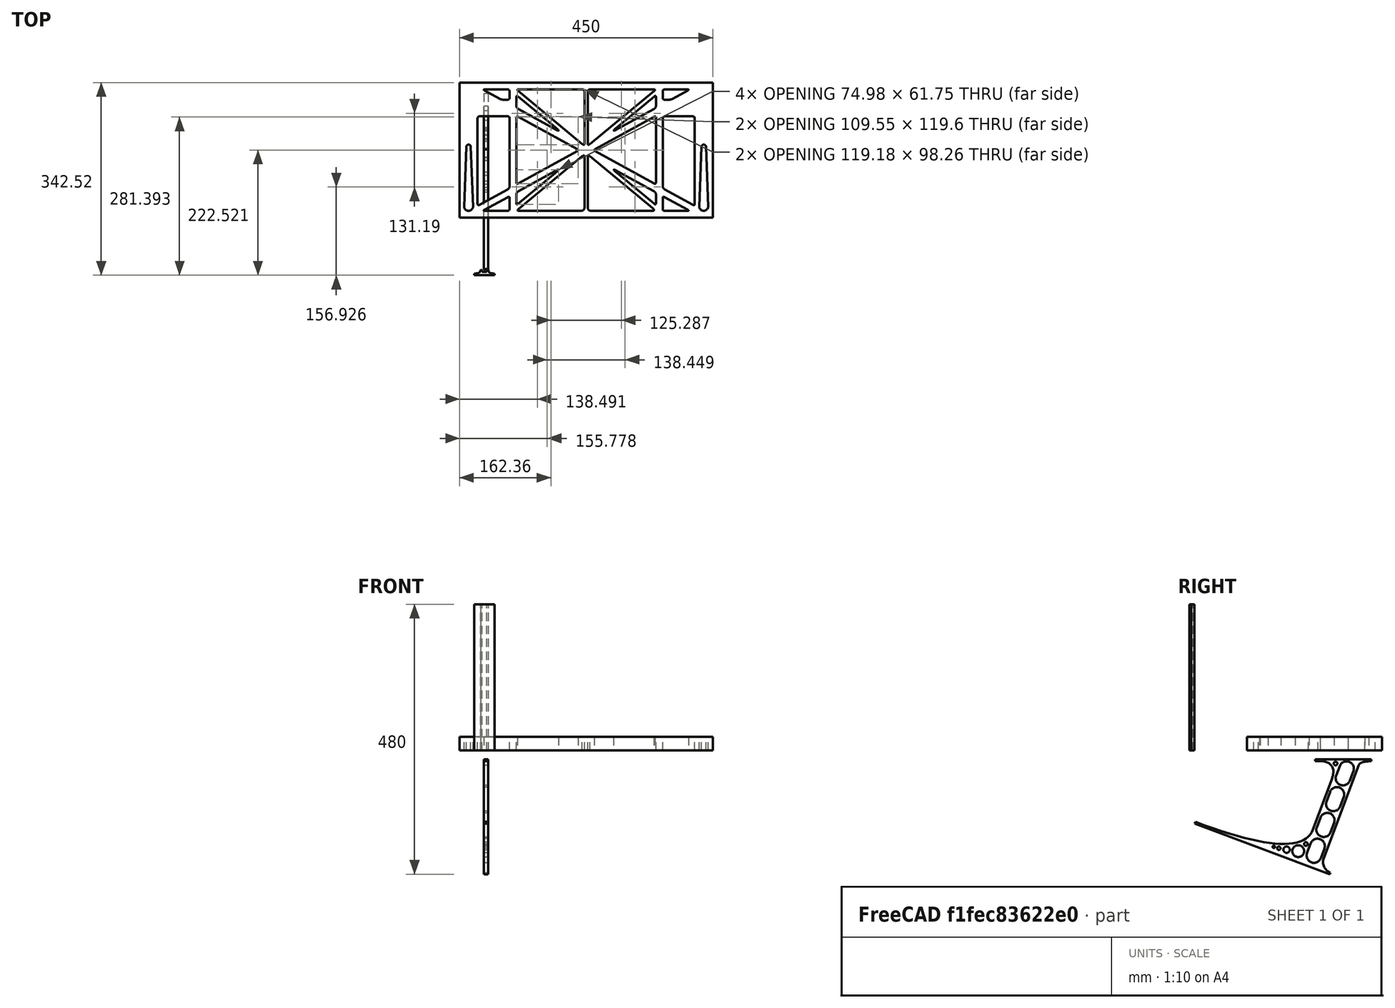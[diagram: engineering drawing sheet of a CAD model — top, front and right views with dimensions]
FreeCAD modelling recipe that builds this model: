
FCSTD DOCUMENT  (FreeCAD 0.19R0.19.2)
Label: laptopStand176FCStd
License: All rights reserved
LicenseURL: http://en.wikipedia.org/wiki/All_rights_reserved
objects: Sketcher::SketchObject×4, Part::Extrusion×3
note: 7 computed .brp shape members not serialized (recipe doc carries the construction recipe); baked Part::Feature solids carry a one-line shape summary decoded from their .brp

FEATURE [Sketcher::SketchObject] Sketch
  FullyConstrained = false
  sketch-geometry (349):
    g0: LineSegment StartX=-10.9272 StartY=-82.7794 StartZ=0 EndX=46.0728 EndY=-51.4823 EndZ=0
    g1: LineSegment StartX=-10.9272 StartY=76.4095 StartZ=0 EndX=-10.9272 EndY=-82.7794 EndZ=0
    g2: LineSegment StartX=46.0728 StartY=76.4095 StartZ=0 EndX=46.0728 EndY=-51.4823 EndZ=0
    g3: LineSegment StartX=-42.9272 StartY=136.221 StartZ=0 EndX=-42.9272 EndY=-103.779 EndZ=0
    g4: LineSegment StartX=407.073 StartY=136.221 StartZ=0 EndX=407.073 EndY=-103.779 EndZ=0
    g5: ArcOfCircle CenterX=-26.9272 CenterY=-83.7794 CenterZ=0 NormalX=0 NormalY=0 NormalZ=1 AngleXU=0 Radius=8 StartAngle=3.14159 EndAngle=6.28319
    g6: ArcOfCircle CenterX=391.073 CenterY=22.1087 CenterZ=0 NormalX=0 NormalY=0 NormalZ=1 AngleXU=0 Radius=8 StartAngle=-4.4e-15 EndAngle=3.14159
    g7: LineSegment StartX=399.073 StartY=22.1087 StartZ=0 EndX=399.073 EndY=-83.7794 EndZ=0
    g8: LineSegment StartX=383.073 StartY=22.1087 StartZ=0 EndX=383.073 EndY=-83.7794 EndZ=0
    g9: ArcOfCircle CenterX=391.073 CenterY=-83.7794 CenterZ=0 NormalX=0 NormalY=0 NormalZ=1 AngleXU=0 Radius=8 StartAngle=3.14159 EndAngle=6.28319
    g10: Circle CenterX=175.022 CenterY=27.0628 CenterZ=0 NormalX=0 NormalY=0 NormalZ=1 AngleXU=0 Radius=1
    g11: Circle CenterX=179.022 CenterY=24.8665 CenterZ=0 NormalX=0 NormalY=0 NormalZ=1 AngleXU=0 Radius=1
    g12: Circle CenterX=179.022 CenterY=27.0628 CenterZ=0 NormalX=0 NormalY=0 NormalZ=1 AngleXU=0 Radius=1
    g13: BSplineCurve PolesCount=3 KnotsCount=2 Degree=2 IsPeriodic=0
    g14: GeomPoint X=175.022 Y=27.0628 Z=0
    g15: GeomPoint X=179.022 Y=27.0628 Z=0
    g16: Circle CenterX=189.124 CenterY=27.0628 CenterZ=0 NormalX=0 NormalY=0 NormalZ=1 AngleXU=0 Radius=1
    g17: Circle CenterX=185.124 CenterY=24.8665 CenterZ=0 NormalX=0 NormalY=0 NormalZ=1 AngleXU=0 Radius=1
    g18: Circle CenterX=185.124 CenterY=27.0628 CenterZ=0 NormalX=0 NormalY=0 NormalZ=1 AngleXU=0 Radius=1
    g19: BSplineCurve PolesCount=3 KnotsCount=2 Degree=2 IsPeriodic=0
    g20: GeomPoint X=189.124 Y=27.0628 Z=0
    g21: GeomPoint X=185.124 Y=27.0628 Z=0
    g22: Circle CenterX=175.022 CenterY=5.37834 CenterZ=0 NormalX=0 NormalY=0 NormalZ=1 AngleXU=0 Radius=1
    g23: Circle CenterX=179.022 CenterY=7.57463 CenterZ=0 NormalX=0 NormalY=0 NormalZ=1 AngleXU=0 Radius=1
    g24: Circle CenterX=179.022 CenterY=5.34704 CenterZ=0 NormalX=0 NormalY=0 NormalZ=1 AngleXU=0 Radius=1
    g25: BSplineCurve PolesCount=3 KnotsCount=2 Degree=2 IsPeriodic=0
    g26: GeomPoint X=175.022 Y=5.37834 Z=0
    g27: GeomPoint X=179.022 Y=5.34704 Z=0
    g28: Circle CenterX=189.124 CenterY=5.37834 CenterZ=0 NormalX=0 NormalY=0 NormalZ=1 AngleXU=0 Radius=1
    g29: Circle CenterX=185.124 CenterY=7.57463 CenterZ=0 NormalX=0 NormalY=0 NormalZ=1 AngleXU=0 Radius=1
    g30: Circle CenterX=185.124 CenterY=5.34704 CenterZ=0 NormalX=0 NormalY=0 NormalZ=1 AngleXU=0 Radius=1
    g31: BSplineCurve PolesCount=3 KnotsCount=2 Degree=2 IsPeriodic=0
    g32: GeomPoint X=189.124 Y=5.37834 Z=0
    g33: GeomPoint X=185.124 Y=5.34704 Z=0
    g34: Circle CenterX=165.871 CenterY=18.1458 CenterZ=0 NormalX=0 NormalY=0 NormalZ=1 AngleXU=0 Radius=1
    g35: Circle CenterX=169.377 CenterY=16.2206 CenterZ=0 NormalX=0 NormalY=0 NormalZ=1 AngleXU=0 Radius=1
    g36: Circle CenterX=165.871 CenterY=14.2954 CenterZ=0 NormalX=0 NormalY=0 NormalZ=1 AngleXU=0 Radius=1
    g37: BSplineCurve PolesCount=3 KnotsCount=2 Degree=2 IsPeriodic=0
    g38: GeomPoint X=165.871 Y=18.1458 Z=0
    g39: GeomPoint X=165.871 Y=14.2954 Z=0
    g40: Circle CenterX=198.275 CenterY=18.1458 CenterZ=0 NormalX=0 NormalY=0 NormalZ=1 AngleXU=0 Radius=1
    g41: Circle CenterX=194.768 CenterY=16.2206 CenterZ=0 NormalX=0 NormalY=0 NormalZ=1 AngleXU=0 Radius=1
    g42: Circle CenterX=198.275 CenterY=14.2954 CenterZ=0 NormalX=0 NormalY=0 NormalZ=1 AngleXU=0 Radius=1
    g43: BSplineCurve PolesCount=3 KnotsCount=2 Degree=2 IsPeriodic=0
    g44: GeomPoint X=198.275 Y=18.1458 Z=0
    g45: GeomPoint X=198.275 Y=14.2954 Z=0
    g46: LineSegment StartX=407.073 StartY=-103.779 StartZ=0 EndX=-42.9272 EndY=-103.779 EndZ=0
    g47: LineSegment StartX=407.073 StartY=136.221 StartZ=0 EndX=-42.9272 EndY=136.221 EndZ=0
    g48: LineSegment StartX=46.0728 StartY=76.4095 StartZ=0 EndX=-10.9272 EndY=76.4095 EndZ=0
    g49: Circle CenterX=125.607 CenterY=54.1951 CenterZ=0 NormalX=0 NormalY=0 NormalZ=1 AngleXU=0 Radius=1
    g50: Circle CenterX=139.632 CenterY=46.4944 CenterZ=0 NormalX=0 NormalY=0 NormalZ=1 AngleXU=0 Radius=1
    g51: Circle CenterX=127.326 CenterY=56.7187 CenterZ=0 NormalX=0 NormalY=0 NormalZ=1 AngleXU=0 Radius=1
    g52: BSplineCurve PolesCount=3 KnotsCount=2 Degree=2 IsPeriodic=0
    g53: GeomPoint X=125.607 Y=54.1951 Z=0
    g54: GeomPoint X=127.326 Y=56.7187 Z=0
    g55: Circle CenterX=236.821 CenterY=56.7187 CenterZ=0 NormalX=0 NormalY=0 NormalZ=1 AngleXU=0 Radius=1
    g56: Circle CenterX=224.513 CenterY=46.4944 CenterZ=0 NormalX=0 NormalY=0 NormalZ=1 AngleXU=0 Radius=1
    g57: Circle CenterX=238.538 CenterY=54.1951 CenterZ=0 NormalX=0 NormalY=0 NormalZ=1 AngleXU=0 Radius=1
    g58: BSplineCurve PolesCount=3 KnotsCount=2 Degree=2 IsPeriodic=0
    g59: GeomPoint X=236.821 Y=56.7187 Z=0
    g60: GeomPoint X=238.538 Y=54.1951 Z=0
    g61: Circle CenterX=238.538 CenterY=-21.7539 CenterZ=0 NormalX=0 NormalY=0 NormalZ=1 AngleXU=0 Radius=1
    g62: Circle CenterX=224.513 CenterY=-14.0532 CenterZ=0 NormalX=0 NormalY=0 NormalZ=1 AngleXU=0 Radius=1
    g63: Circle CenterX=236.821 CenterY=-24.2775 CenterZ=0 NormalX=0 NormalY=0 NormalZ=1 AngleXU=0 Radius=1
    g64: BSplineCurve PolesCount=3 KnotsCount=2 Degree=2 IsPeriodic=0
    g65: GeomPoint X=238.538 Y=-21.7539 Z=0
    g66: GeomPoint X=236.821 Y=-24.2775 Z=0
    g67: Circle CenterX=125.607 CenterY=-21.7539 CenterZ=0 NormalX=0 NormalY=0 NormalZ=1 AngleXU=0 Radius=1
    g68: Circle CenterX=139.632 CenterY=-14.0532 CenterZ=0 NormalX=0 NormalY=0 NormalZ=1 AngleXU=0 Radius=1
    g69: Circle CenterX=127.325 CenterY=-24.2775 CenterZ=0 NormalX=0 NormalY=0 NormalZ=1 AngleXU=0 Radius=1
    g70: BSplineCurve PolesCount=3 KnotsCount=2 Degree=2 IsPeriodic=0
    g71: GeomPoint X=125.607 Y=-21.7539 Z=0
    g72: GeomPoint X=127.325 Y=-24.2775 Z=0
    g73: Circle CenterX=302.996 CenterY=111.695 CenterZ=0 NormalX=0 NormalY=0 NormalZ=1 AngleXU=0 Radius=1
    g74: Circle CenterX=306.073 CenterY=114.251 CenterZ=0 NormalX=0 NormalY=0 NormalZ=1 AngleXU=0 Radius=1
    g75: Circle CenterX=306.073 CenterY=110.251 CenterZ=0 NormalX=0 NormalY=0 NormalZ=1 AngleXU=0 Radius=1
    g76: BSplineCurve PolesCount=3 KnotsCount=2 Degree=2 IsPeriodic=0
    g77: GeomPoint X=302.996 Y=111.695 Z=0
    g78: GeomPoint X=306.073 Y=110.251 Z=0
    g79: Circle CenterX=306.073 CenterY=95.2763 CenterZ=0 NormalX=0 NormalY=0 NormalZ=1 AngleXU=0 Radius=1
    g80: Circle CenterX=306.073 CenterY=91.2763 CenterZ=0 NormalX=0 NormalY=0 NormalZ=1 AngleXU=0 Radius=1
    g81: Circle CenterX=302.567 CenterY=89.3511 CenterZ=0 NormalX=0 NormalY=0 NormalZ=1 AngleXU=0 Radius=1
    g82: BSplineCurve PolesCount=3 KnotsCount=2 Degree=2 IsPeriodic=0
    g83: GeomPoint X=306.073 Y=95.2763 Z=0
    g84: GeomPoint X=302.567 Y=89.3511 Z=0
    g85: LineSegment StartX=306.073 StartY=110.251 StartZ=0 EndX=306.073 EndY=95.2763 EndZ=0
    g86: LineSegment StartX=302.996 StartY=111.695 StartZ=0 EndX=236.821 EndY=56.7187 EndZ=0
    g87: LineSegment StartX=238.538 StartY=54.1951 StartZ=0 EndX=302.567 EndY=89.3511 EndZ=0
    g88: Circle CenterX=61.1496 CenterY=111.695 CenterZ=0 NormalX=0 NormalY=0 NormalZ=1 AngleXU=0 Radius=1
    g89: Circle CenterX=58.0728 CenterY=114.251 CenterZ=0 NormalX=0 NormalY=0 NormalZ=1 AngleXU=0 Radius=1
    g90: Circle CenterX=58.0728 CenterY=110.251 CenterZ=0 NormalX=0 NormalY=0 NormalZ=1 AngleXU=0 Radius=1
    g91: BSplineCurve PolesCount=3 KnotsCount=2 Degree=2 IsPeriodic=0
    g92: GeomPoint X=61.1496 Y=111.695 Z=0
    g93: GeomPoint X=58.0728 Y=110.251 Z=0
    g94: Circle CenterX=61.5791 CenterY=89.3511 CenterZ=0 NormalX=0 NormalY=0 NormalZ=1 AngleXU=0 Radius=1
    g95: Circle CenterX=58.0728 CenterY=91.2763 CenterZ=0 NormalX=0 NormalY=0 NormalZ=1 AngleXU=0 Radius=1
    g96: Circle CenterX=58.0728 CenterY=95.2763 CenterZ=0 NormalX=0 NormalY=0 NormalZ=1 AngleXU=0 Radius=1
    g97: BSplineCurve PolesCount=3 KnotsCount=2 Degree=2 IsPeriodic=0
    g98: GeomPoint X=61.5791 Y=89.3511 Z=0
    g99: GeomPoint X=58.0728 Y=95.2763 Z=0
    g100: LineSegment StartX=58.0728 StartY=110.251 StartZ=0 EndX=58.0728 EndY=95.2763 EndZ=0
    g101: LineSegment StartX=61.1496 StartY=111.695 StartZ=0 EndX=127.326 EndY=56.7187 EndZ=0
    g102: LineSegment StartX=125.607 StartY=54.1951 StartZ=0 EndX=61.5791 EndY=89.3511 EndZ=0
    g103: Circle CenterX=61.5791 CenterY=-56.9099 CenterZ=0 NormalX=0 NormalY=0 NormalZ=1 AngleXU=0 Radius=1
    g104: Circle CenterX=58.0728 CenterY=-58.8351 CenterZ=0 NormalX=0 NormalY=0 NormalZ=1 AngleXU=0 Radius=1
    g105: Circle CenterX=58.0728 CenterY=-62.8351 CenterZ=0 NormalX=0 NormalY=0 NormalZ=1 AngleXU=0 Radius=1
    g106: BSplineCurve PolesCount=3 KnotsCount=2 Degree=2 IsPeriodic=0
    g107: GeomPoint X=61.5791 Y=-56.9099 Z=0
    g108: GeomPoint X=58.0728 Y=-62.8351 Z=0
    g109: Circle CenterX=58.0728 CenterY=-77.8102 CenterZ=0 NormalX=0 NormalY=0 NormalZ=1 AngleXU=0 Radius=1
    g110: Circle CenterX=58.0728 CenterY=-81.8102 CenterZ=0 NormalX=0 NormalY=0 NormalZ=1 AngleXU=0 Radius=1
    g111: Circle CenterX=61.1496 CenterY=-79.2541 CenterZ=0 NormalX=0 NormalY=0 NormalZ=1 AngleXU=0 Radius=1
    g112: BSplineCurve PolesCount=3 KnotsCount=2 Degree=2 IsPeriodic=0
    g113: GeomPoint X=58.0728 Y=-77.8102 Z=0
    g114: GeomPoint X=61.1496 Y=-79.2541 Z=0
    g115: LineSegment StartX=58.0728 StartY=-62.8351 StartZ=0 EndX=58.0728 EndY=-77.8102 EndZ=0
    g116: LineSegment StartX=61.1496 StartY=-79.2541 StartZ=0 EndX=127.325 EndY=-24.2775 EndZ=0
    g117: LineSegment StartX=125.607 StartY=-21.7539 StartZ=0 EndX=61.5791 EndY=-56.9099 EndZ=0
    g118: Circle CenterX=302.567 CenterY=-56.9099 CenterZ=0 NormalX=0 NormalY=0 NormalZ=1 AngleXU=0 Radius=1
    g119: Circle CenterX=306.073 CenterY=-58.8351 CenterZ=0 NormalX=0 NormalY=0 NormalZ=1 AngleXU=0 Radius=1
    g120: Circle CenterX=306.073 CenterY=-62.8351 CenterZ=0 NormalX=0 NormalY=0 NormalZ=1 AngleXU=0 Radius=1
    g121: BSplineCurve PolesCount=3 KnotsCount=2 Degree=2 IsPeriodic=0
    g122: GeomPoint X=302.567 Y=-56.9099 Z=0
    g123: GeomPoint X=306.073 Y=-62.8351 Z=0
    g124: Circle CenterX=302.996 CenterY=-79.2541 CenterZ=0 NormalX=0 NormalY=0 NormalZ=1 AngleXU=0 Radius=1
    g125: Circle CenterX=306.073 CenterY=-81.8102 CenterZ=0 NormalX=0 NormalY=0 NormalZ=1 AngleXU=0 Radius=1
    g126: Circle CenterX=306.073 CenterY=-77.8102 CenterZ=0 NormalX=0 NormalY=0 NormalZ=1 AngleXU=0 Radius=1
    g127: BSplineCurve PolesCount=3 KnotsCount=2 Degree=2 IsPeriodic=0
    g128: GeomPoint X=302.996 Y=-79.2541 Z=0
    g129: GeomPoint X=306.073 Y=-77.8102 Z=0
    g130: LineSegment StartX=306.073 StartY=-62.8351 StartZ=0 EndX=306.073 EndY=-77.8102 EndZ=0
    g131: LineSegment StartX=302.996 StartY=-79.2541 StartZ=0 EndX=236.821 EndY=-24.2775 EndZ=0
    g132: LineSegment StartX=238.538 StartY=-21.7539 StartZ=0 EndX=302.567 EndY=-56.9099 EndZ=0
    g133: Circle CenterX=61.6457 CenterY=-88.8112 CenterZ=0 NormalX=0 NormalY=0 NormalZ=1 AngleXU=0 Radius=1
    g134: Circle CenterX=58.0728 CenterY=-91.7794 CenterZ=0 NormalX=0 NormalY=0 NormalZ=1 AngleXU=0 Radius=1
    g135: Circle CenterX=63.9135 CenterY=-91.7794 CenterZ=0 NormalX=0 NormalY=0 NormalZ=1 AngleXU=0 Radius=1
    g136: BSplineCurve PolesCount=3 KnotsCount=2 Degree=2 IsPeriodic=0
    g137: GeomPoint X=61.6457 Y=-88.8112 Z=0
    g138: GeomPoint X=63.9135 Y=-91.7794 Z=0
    g139: Circle CenterX=179.022 CenterY=-85.8163 CenterZ=0 NormalX=0 NormalY=0 NormalZ=1 AngleXU=0 Radius=1
    g140: Circle CenterX=179.022 CenterY=-91.7794 CenterZ=0 NormalX=0 NormalY=0 NormalZ=1 AngleXU=0 Radius=1
    g141: Circle CenterX=171.895 CenterY=-91.7794 CenterZ=0 NormalX=0 NormalY=0 NormalZ=1 AngleXU=0 Radius=1
    g142: BSplineCurve PolesCount=3 KnotsCount=2 Degree=2 IsPeriodic=0
    g143: GeomPoint X=179.022 Y=-85.8163 Z=0
    g144: GeomPoint X=171.895 Y=-91.7794 Z=0
    g145: Circle CenterX=185.124 CenterY=-86.2028 CenterZ=0 NormalX=0 NormalY=0 NormalZ=1 AngleXU=0 Radius=1
    g146: Circle CenterX=185.124 CenterY=-91.7794 CenterZ=0 NormalX=0 NormalY=0 NormalZ=1 AngleXU=0 Radius=1
    g147: Circle CenterX=191.747 CenterY=-91.7794 CenterZ=0 NormalX=0 NormalY=0 NormalZ=1 AngleXU=0 Radius=1
    g148: BSplineCurve PolesCount=3 KnotsCount=2 Degree=2 IsPeriodic=0
    g149: GeomPoint X=185.124 Y=-86.2028 Z=0
    g150: GeomPoint X=191.747 Y=-91.7794 Z=0
    g151: Circle CenterX=299.888 CenterY=-86.6413 CenterZ=0 NormalX=0 NormalY=0 NormalZ=1 AngleXU=0 Radius=1
    g152: Circle CenterX=306.073 CenterY=-91.7794 CenterZ=0 NormalX=0 NormalY=0 NormalZ=1 AngleXU=0 Radius=1
    g153: Circle CenterX=298.776 CenterY=-91.7794 CenterZ=0 NormalX=0 NormalY=0 NormalZ=1 AngleXU=0 Radius=1
    g154: BSplineCurve PolesCount=3 KnotsCount=2 Degree=2 IsPeriodic=0
    g155: GeomPoint X=299.888 Y=-86.6413 Z=0
    g156: GeomPoint X=298.776 Y=-91.7794 Z=0
    g157: LineSegment StartX=189.124 StartY=5.37834 StartZ=0 EndX=299.888 EndY=-86.6413 EndZ=0
    g158: LineSegment StartX=298.776 StartY=-91.7794 StartZ=0 EndX=191.747 EndY=-91.7794 EndZ=0
    g159: LineSegment StartX=185.124 StartY=-86.2028 StartZ=0 EndX=185.124 EndY=5.34704 EndZ=0
    g160: LineSegment StartX=179.022 StartY=5.34704 StartZ=0 EndX=179.022 EndY=-85.8163 EndZ=0
    g161: LineSegment StartX=171.895 StartY=-91.7794 StartZ=0 EndX=63.9135 EndY=-91.7794 EndZ=0
    g162: LineSegment StartX=61.6457 StartY=-88.8112 StartZ=0 EndX=175.022 EndY=5.37834 EndZ=0
    g163: Circle CenterX=302.073 CenterY=124.221 CenterZ=0 NormalX=0 NormalY=0 NormalZ=1 AngleXU=0 Radius=1
    g164: Circle CenterX=306.073 CenterY=124.221 CenterZ=0 NormalX=0 NormalY=0 NormalZ=1 AngleXU=0 Radius=1
    g165: Circle CenterX=302.996 CenterY=121.665 CenterZ=0 NormalX=0 NormalY=0 NormalZ=1 AngleXU=0 Radius=1
    g166: BSplineCurve PolesCount=3 KnotsCount=2 Degree=2 IsPeriodic=0
    g167: GeomPoint X=302.073 Y=124.221 Z=0
    g168: GeomPoint X=302.996 Y=121.665 Z=0
    g169: Circle CenterX=189.124 CenterY=124.221 CenterZ=0 NormalX=0 NormalY=0 NormalZ=1 AngleXU=0 Radius=1
    g170: Circle CenterX=185.124 CenterY=124.221 CenterZ=0 NormalX=0 NormalY=0 NormalZ=1 AngleXU=0 Radius=1
    g171: Circle CenterX=185.124 CenterY=120.221 CenterZ=0 NormalX=0 NormalY=0 NormalZ=1 AngleXU=0 Radius=1
    g172: BSplineCurve PolesCount=3 KnotsCount=2 Degree=2 IsPeriodic=0
    g173: GeomPoint X=189.124 Y=124.221 Z=0
    g174: GeomPoint X=185.124 Y=120.221 Z=0
    g175: Circle CenterX=175.022 CenterY=124.221 CenterZ=0 NormalX=0 NormalY=0 NormalZ=1 AngleXU=0 Radius=1
    g176: Circle CenterX=179.022 CenterY=124.221 CenterZ=0 NormalX=0 NormalY=0 NormalZ=1 AngleXU=0 Radius=1
    g177: Circle CenterX=179.022 CenterY=120.221 CenterZ=0 NormalX=0 NormalY=0 NormalZ=1 AngleXU=0 Radius=1
    g178: BSplineCurve PolesCount=3 KnotsCount=2 Degree=2 IsPeriodic=0
    g179: GeomPoint X=175.022 Y=124.221 Z=0
    g180: GeomPoint X=179.022 Y=120.221 Z=0
    g181: Circle CenterX=62.0728 CenterY=124.221 CenterZ=0 NormalX=0 NormalY=0 NormalZ=1 AngleXU=0 Radius=1
    g182: Circle CenterX=58.0728 CenterY=124.221 CenterZ=0 NormalX=0 NormalY=0 NormalZ=1 AngleXU=0 Radius=1
    g183: Circle CenterX=61.1496 CenterY=121.665 CenterZ=0 NormalX=0 NormalY=0 NormalZ=1 AngleXU=0 Radius=1
    g184: BSplineCurve PolesCount=3 KnotsCount=2 Degree=2 IsPeriodic=0
    g185: GeomPoint X=62.0728 Y=124.221 Z=0
    g186: GeomPoint X=61.1496 Y=121.665 Z=0
    g187: LineSegment StartX=62.0728 StartY=124.221 StartZ=0 EndX=175.022 EndY=124.221 EndZ=0
    g188: LineSegment StartX=179.022 StartY=120.221 StartZ=0 EndX=179.022 EndY=27.0628 EndZ=0
    g189: LineSegment StartX=185.124 StartY=27.0628 StartZ=0 EndX=185.124 EndY=120.221 EndZ=0
    g190: LineSegment StartX=189.124 StartY=124.221 StartZ=0 EndX=302.073 EndY=124.221 EndZ=0
    g191: LineSegment StartX=302.996 StartY=121.665 StartZ=0 EndX=189.124 EndY=27.0628 EndZ=0
    g192: LineSegment StartX=175.022 StartY=27.0628 StartZ=0 EndX=61.1496 EndY=121.665 EndZ=0
    g193: Circle CenterX=61.5791 CenterY=75.4095 CenterZ=0 NormalX=0 NormalY=0 NormalZ=1 AngleXU=0 Radius=1
    g194: Circle CenterX=58.0728 CenterY=77.3346 CenterZ=0 NormalX=0 NormalY=0 NormalZ=1 AngleXU=0 Radius=1
    g195: Circle CenterX=58.0728 CenterY=73.3346 CenterZ=0 NormalX=0 NormalY=0 NormalZ=1 AngleXU=0 Radius=1
    g196: BSplineCurve PolesCount=3 KnotsCount=2 Degree=2 IsPeriodic=0
    g197: GeomPoint X=61.5791 Y=75.4095 Z=0
    g198: GeomPoint X=58.0728 Y=73.3346 Z=0
    g199: Circle CenterX=58.0728 CenterY=-40.8935 CenterZ=0 NormalX=0 NormalY=0 NormalZ=1 AngleXU=0 Radius=1
    g200: Circle CenterX=58.0728 CenterY=-44.8935 CenterZ=0 NormalX=0 NormalY=0 NormalZ=1 AngleXU=0 Radius=1
    g201: Circle CenterX=61.5791 CenterY=-42.9683 CenterZ=0 NormalX=0 NormalY=0 NormalZ=1 AngleXU=0 Radius=1
    g202: BSplineCurve PolesCount=3 KnotsCount=2 Degree=2 IsPeriodic=0
    g203: GeomPoint X=58.0728 Y=-40.8935 Z=0
    g204: GeomPoint X=61.5791 Y=-42.9683 Z=0
    g205: LineSegment StartX=61.5791 StartY=-42.9683 StartZ=0 EndX=165.871 EndY=14.2954 EndZ=0
    g206: LineSegment StartX=165.871 StartY=18.1458 StartZ=0 EndX=61.5791 EndY=75.4095 EndZ=0
    g207: LineSegment StartX=58.0728 StartY=73.3346 StartZ=0 EndX=58.0728 EndY=-40.8935 EndZ=0
    g208: Circle CenterX=302.567 CenterY=-42.9683 CenterZ=0 NormalX=0 NormalY=0 NormalZ=1 AngleXU=0 Radius=1
    g209: Circle CenterX=306.073 CenterY=-44.8935 CenterZ=0 NormalX=0 NormalY=0 NormalZ=1 AngleXU=0 Radius=1
    g210: Circle CenterX=306.073 CenterY=-40.8935 CenterZ=0 NormalX=0 NormalY=0 NormalZ=1 AngleXU=0 Radius=1
    g211: BSplineCurve PolesCount=3 KnotsCount=2 Degree=2 IsPeriodic=0
    g212: GeomPoint X=302.567 Y=-42.9683 Z=0
    g213: GeomPoint X=306.073 Y=-40.8935 Z=0
    g214: Circle CenterX=306.073 CenterY=73.3346 CenterZ=0 NormalX=0 NormalY=0 NormalZ=1 AngleXU=0 Radius=1
    g215: Circle CenterX=306.073 CenterY=77.3346 CenterZ=0 NormalX=0 NormalY=0 NormalZ=1 AngleXU=0 Radius=1
    g216: Circle CenterX=302.567 CenterY=75.4095 CenterZ=0 NormalX=0 NormalY=0 NormalZ=1 AngleXU=0 Radius=1
    g217: BSplineCurve PolesCount=3 KnotsCount=2 Degree=2 IsPeriodic=0
    g218: GeomPoint X=306.073 Y=73.3346 Z=0
    g219: GeomPoint X=302.567 Y=75.4095 Z=0
    g220: LineSegment StartX=302.567 StartY=-42.9683 StartZ=0 EndX=198.275 EndY=14.2954 EndZ=0
    g221: LineSegment StartX=198.275 StartY=18.1458 StartZ=0 EndX=302.567 EndY=75.4095 EndZ=0
    g222: LineSegment StartX=306.073 StartY=73.3346 StartZ=0 EndX=306.073 EndY=-40.8935 EndZ=0
    g223: LineSegment StartX=322.073 StartY=105.865 StartZ=0 EndX=328.643 EndY=105.865 EndZ=0
    g224: LineSegment StartX=318.073 StartY=120.221 StartZ=0 EndX=318.073 EndY=109.865 EndZ=0
    g225: LineSegment StartX=336.157 StartY=107.779 StartZ=0 EndX=362.567 EndY=122.294 EndZ=0
    g226: Circle CenterX=362.073 CenterY=124.221 CenterZ=0 NormalX=0 NormalY=0 NormalZ=1 AngleXU=0 Radius=1
    g227: Circle CenterX=366.073 CenterY=124.221 CenterZ=0 NormalX=0 NormalY=0 NormalZ=1 AngleXU=0 Radius=1
    g228: Circle CenterX=362.567 CenterY=122.294 CenterZ=0 NormalX=0 NormalY=0 NormalZ=1 AngleXU=0 Radius=1
    g229: BSplineCurve PolesCount=3 KnotsCount=2 Degree=2 IsPeriodic=0
    g230: GeomPoint X=362.073 Y=124.221 Z=0
    g231: GeomPoint X=362.567 Y=122.294 Z=0
    g232: Circle CenterX=322.073 CenterY=124.221 CenterZ=0 NormalX=0 NormalY=0 NormalZ=1 AngleXU=0 Radius=1
    g233: Circle CenterX=318.073 CenterY=124.221 CenterZ=0 NormalX=0 NormalY=0 NormalZ=1 AngleXU=0 Radius=1
    g234: Circle CenterX=318.073 CenterY=120.221 CenterZ=0 NormalX=0 NormalY=0 NormalZ=1 AngleXU=0 Radius=1
    g235: BSplineCurve PolesCount=3 KnotsCount=2 Degree=2 IsPeriodic=0
    g236: GeomPoint X=322.073 Y=124.221 Z=0
    g237: GeomPoint X=318.073 Y=120.221 Z=0
    g238: Circle CenterX=322.073 CenterY=105.865 CenterZ=0 NormalX=0 NormalY=0 NormalZ=1 AngleXU=0 Radius=1
    g239: Circle CenterX=318.073 CenterY=105.865 CenterZ=0 NormalX=0 NormalY=0 NormalZ=1 AngleXU=0 Radius=1
    g240: Circle CenterX=318.073 CenterY=109.865 CenterZ=0 NormalX=0 NormalY=0 NormalZ=1 AngleXU=0 Radius=1
    g241: BSplineCurve PolesCount=3 KnotsCount=2 Degree=2 IsPeriodic=0
    g242: GeomPoint X=322.073 Y=105.865 Z=0
    g243: GeomPoint X=318.073 Y=109.865 Z=0
    g244: Circle CenterX=336.157 CenterY=107.779 CenterZ=0 NormalX=0 NormalY=0 NormalZ=1 AngleXU=0 Radius=1
    g245: Circle CenterX=332.651 CenterY=105.853 CenterZ=0 NormalX=0 NormalY=0 NormalZ=1 AngleXU=0 Radius=1
    g246: Circle CenterX=328.643 CenterY=105.865 CenterZ=0 NormalX=0 NormalY=0 NormalZ=1 AngleXU=0 Radius=1
    g247: BSplineCurve PolesCount=3 KnotsCount=2 Degree=2 IsPeriodic=0
    g248: GeomPoint X=336.157 Y=107.779 Z=0
    g249: GeomPoint X=328.643 Y=105.865 Z=0
    g250: LineSegment StartX=322.073 StartY=124.221 StartZ=0 EndX=362.073 EndY=124.221 EndZ=0
    g251: Circle CenterX=371.567 CenterY=-80.8644 CenterZ=0 NormalX=0 NormalY=0 NormalZ=1 AngleXU=0 Radius=1
    g252: Circle CenterX=375.073 CenterY=-82.7896 CenterZ=0 NormalX=0 NormalY=0 NormalZ=1 AngleXU=0 Radius=1
    g253: Circle CenterX=375.073 CenterY=-78.7896 CenterZ=0 NormalX=0 NormalY=0 NormalZ=1 AngleXU=0 Radius=1
    g254: BSplineCurve PolesCount=3 KnotsCount=2 Degree=2 IsPeriodic=0
    g255: GeomPoint X=371.567 Y=-80.8644 Z=0
    g256: GeomPoint X=375.073 Y=-78.7896 Z=0
    g257: Circle CenterX=321.579 CenterY=-53.4075 CenterZ=0 NormalX=0 NormalY=0 NormalZ=1 AngleXU=0 Radius=1
    g258: Circle CenterX=318.073 CenterY=-51.4823 CenterZ=0 NormalX=0 NormalY=0 NormalZ=1 AngleXU=0 Radius=1
    g259: Circle CenterX=318.073 CenterY=-47.4805 CenterZ=0 NormalX=0 NormalY=0 NormalZ=1 AngleXU=0 Radius=1
    g260: BSplineCurve PolesCount=3 KnotsCount=2 Degree=2 IsPeriodic=0
    g261: GeomPoint X=321.579 Y=-53.4075 Z=0
    g262: GeomPoint X=318.073 Y=-47.4805 Z=0
    g263: LineSegment StartX=371.567 StartY=-80.8644 StartZ=0 EndX=321.579 EndY=-53.4075 EndZ=0
    g264: Circle CenterX=321.579 CenterY=-67.3492 CenterZ=0 NormalX=0 NormalY=0 NormalZ=1 AngleXU=0 Radius=1
    g265: Circle CenterX=318.073 CenterY=-65.424 CenterZ=0 NormalX=0 NormalY=0 NormalZ=1 AngleXU=0 Radius=1
    g266: Circle CenterX=318.073 CenterY=-69.424 CenterZ=0 NormalX=0 NormalY=0 NormalZ=1 AngleXU=0 Radius=1
    g267: BSplineCurve PolesCount=3 KnotsCount=2 Degree=2 IsPeriodic=0
    g268: GeomPoint X=321.579 Y=-67.3492 Z=0
    g269: GeomPoint X=318.073 Y=-69.424 Z=0
    g270: Circle CenterX=362.567 CenterY=-89.8542 CenterZ=0 NormalX=0 NormalY=0 NormalZ=1 AngleXU=0 Radius=1
    g271: Circle CenterX=366.073 CenterY=-91.7794 CenterZ=0 NormalX=0 NormalY=0 NormalZ=1 AngleXU=0 Radius=1
    g272: Circle CenterX=362.073 CenterY=-91.7794 CenterZ=0 NormalX=0 NormalY=0 NormalZ=1 AngleXU=0 Radius=1
    g273: BSplineCurve PolesCount=3 KnotsCount=2 Degree=2 IsPeriodic=0
    g274: GeomPoint X=362.567 Y=-89.8542 Z=0
    g275: GeomPoint X=362.073 Y=-91.7794 Z=0
    g276: Circle CenterX=322.073 CenterY=-91.7794 CenterZ=0 NormalX=0 NormalY=0 NormalZ=1 AngleXU=0 Radius=1
    g277: Circle CenterX=318.073 CenterY=-91.7794 CenterZ=0 NormalX=0 NormalY=0 NormalZ=1 AngleXU=0 Radius=1
    g278: Circle CenterX=318.073 CenterY=-87.7794 CenterZ=0 NormalX=0 NormalY=0 NormalZ=1 AngleXU=0 Radius=1
    g279: BSplineCurve PolesCount=3 KnotsCount=2 Degree=2 IsPeriodic=0
    g280: GeomPoint X=322.073 Y=-91.7794 Z=0
    g281: GeomPoint X=318.073 Y=-87.7794 Z=0
    g282: LineSegment StartX=362.567 StartY=-89.8542 StartZ=0 EndX=321.579 EndY=-67.3492 EndZ=0
    g283: LineSegment StartX=318.073 StartY=-69.424 StartZ=0 EndX=318.073 EndY=-87.7794 EndZ=0
    g284: LineSegment StartX=322.073 StartY=-91.7794 StartZ=0 EndX=362.073 EndY=-91.7794 EndZ=0
    g285: Circle CenterX=2.07281 CenterY=124.221 CenterZ=0 NormalX=0 NormalY=0 NormalZ=1 AngleXU=0 Radius=1
    g286: Circle CenterX=1.57905 CenterY=122.295 CenterZ=0 NormalX=0 NormalY=0 NormalZ=1 AngleXU=0 Radius=1
    g287: BSplineCurve PolesCount=3 KnotsCount=2 Degree=2 IsPeriodic=0
    g288: GeomPoint X=2.07281 Y=124.221 Z=0
    g289: GeomPoint X=1.57905 Y=122.295 Z=0
    g290: Circle CenterX=42.0728 CenterY=124.221 CenterZ=0 NormalX=0 NormalY=0 NormalZ=1 AngleXU=0 Radius=1
    g291: Circle CenterX=46.0728 CenterY=124.221 CenterZ=0 NormalX=0 NormalY=0 NormalZ=1 AngleXU=0 Radius=1
    g292: Circle CenterX=46.0728 CenterY=120.221 CenterZ=0 NormalX=0 NormalY=0 NormalZ=1 AngleXU=0 Radius=1
    g293: BSplineCurve PolesCount=3 KnotsCount=2 Degree=2 IsPeriodic=0
    g294: GeomPoint X=42.0728 Y=124.221 Z=0
    g295: GeomPoint X=46.0728 Y=120.221 Z=0
    g296: Circle CenterX=46.0728 CenterY=109.865 CenterZ=0 NormalX=0 NormalY=0 NormalZ=1 AngleXU=0 Radius=1
    g297: Circle CenterX=46.0728 CenterY=105.865 CenterZ=0 NormalX=0 NormalY=0 NormalZ=1 AngleXU=0 Radius=1
    g298: Circle CenterX=42.0728 CenterY=105.865 CenterZ=0 NormalX=0 NormalY=0 NormalZ=1 AngleXU=0 Radius=1
    g299: BSplineCurve PolesCount=3 KnotsCount=2 Degree=2 IsPeriodic=0
    g300: GeomPoint X=46.0728 Y=109.865 Z=0
    g301: GeomPoint X=42.0728 Y=105.865 Z=0
    g302: Circle CenterX=35.5028 CenterY=105.865 CenterZ=0 NormalX=0 NormalY=0 NormalZ=1 AngleXU=0 Radius=1
    g303: Circle CenterX=31.5028 CenterY=105.865 CenterZ=0 NormalX=0 NormalY=0 NormalZ=1 AngleXU=0 Radius=1
    g304: Circle CenterX=27.9965 CenterY=107.79 CenterZ=0 NormalX=0 NormalY=0 NormalZ=1 AngleXU=0 Radius=1
    g305: BSplineCurve PolesCount=3 KnotsCount=2 Degree=2 IsPeriodic=0
    g306: GeomPoint X=35.5028 Y=105.865 Z=0
    g307: GeomPoint X=27.9965 Y=107.79 Z=0
    g308: LineSegment StartX=2.07281 StartY=124.221 StartZ=0 EndX=42.0728 EndY=124.221 EndZ=0
    g309: LineSegment StartX=46.0728 StartY=120.221 StartZ=0 EndX=46.0728 EndY=109.865 EndZ=0
    g310: LineSegment StartX=42.0728 StartY=105.865 StartZ=0 EndX=35.5028 EndY=105.865 EndZ=0
    g311: LineSegment StartX=27.9965 StartY=107.79 StartZ=0 EndX=1.57905 EndY=122.295 EndZ=0
    g312: Circle CenterX=42.5666 CenterY=-67.3492 CenterZ=0 NormalX=0 NormalY=0 NormalZ=1 AngleXU=0 Radius=1
    g313: Circle CenterX=46.0728 CenterY=-65.424 CenterZ=0 NormalX=0 NormalY=0 NormalZ=1 AngleXU=0 Radius=1
    g314: Circle CenterX=46.0728 CenterY=-69.424 CenterZ=0 NormalX=0 NormalY=0 NormalZ=1 AngleXU=0 Radius=1
    g315: BSplineCurve PolesCount=3 KnotsCount=2 Degree=2 IsPeriodic=0
    g316: GeomPoint X=42.5666 Y=-67.3492 Z=0
    g317: GeomPoint X=46.0728 Y=-69.424 Z=0
    g318: Circle CenterX=46.0728 CenterY=-87.7794 CenterZ=0 NormalX=0 NormalY=0 NormalZ=1 AngleXU=0 Radius=1
    g319: Circle CenterX=46.0728 CenterY=-91.7794 CenterZ=0 NormalX=0 NormalY=0 NormalZ=1 AngleXU=0 Radius=1
    g320: Circle CenterX=42.0728 CenterY=-91.7794 CenterZ=0 NormalX=0 NormalY=0 NormalZ=1 AngleXU=0 Radius=1
    g321: BSplineCurve PolesCount=3 KnotsCount=2 Degree=2 IsPeriodic=0
    g322: GeomPoint X=46.0728 Y=-87.7794 Z=0
    g323: GeomPoint X=42.0728 Y=-91.7794 Z=0
    g324: Circle CenterX=2.07281 CenterY=-91.7794 CenterZ=0 NormalX=0 NormalY=0 NormalZ=1 AngleXU=0 Radius=1
    g325: Circle CenterX=-1.92719 CenterY=-91.7794 CenterZ=0 NormalX=0 NormalY=0 NormalZ=1 AngleXU=0 Radius=1
    g326: Circle CenterX=1.57905 CenterY=-89.8542 CenterZ=0 NormalX=0 NormalY=0 NormalZ=1 AngleXU=0 Radius=1
    g327: BSplineCurve PolesCount=3 KnotsCount=2 Degree=2 IsPeriodic=0
    g328: GeomPoint X=2.07281 Y=-91.7794 Z=0
    g329: GeomPoint X=1.57905 Y=-89.8542 Z=0
    g330: LineSegment StartX=2.07281 StartY=-91.7794 StartZ=0 EndX=42.0728 EndY=-91.7794 EndZ=0
    g331: LineSegment StartX=46.0728 StartY=-87.7794 StartZ=0 EndX=46.0728 EndY=-69.424 EndZ=0
    g332: LineSegment StartX=42.5666 StartY=-67.3492 StartZ=0 EndX=1.57905 EndY=-89.8542 EndZ=0
    g333: Circle CenterX=322.073 CenterY=76.4095 CenterZ=0 NormalX=0 NormalY=0 NormalZ=1 AngleXU=0 Radius=4
    g334: BSplineCurve PolesCount=3 KnotsCount=2 Degree=2 IsPeriodic=0
    g335: GeomPoint X=318.073 Y=72.4095 Z=0
    g336: GeomPoint X=322.073 Y=76.4095 Z=0
    g337: Circle CenterX=375.073 CenterY=72.4095 CenterZ=0 NormalX=0 NormalY=0 NormalZ=1 AngleXU=0 Radius=1
    g338: Circle CenterX=375.073 CenterY=76.4095 CenterZ=0 NormalX=0 NormalY=0 NormalZ=1 AngleXU=0 Radius=1
    g339: Circle CenterX=371.073 CenterY=76.4095 CenterZ=0 NormalX=0 NormalY=0 NormalZ=1 AngleXU=0 Radius=1
    g340: BSplineCurve PolesCount=3 KnotsCount=2 Degree=2 IsPeriodic=0
    g341: GeomPoint X=375.073 Y=72.4095 Z=0
    g342: GeomPoint X=371.073 Y=76.4095 Z=0
    g343: LineSegment StartX=322.073 StartY=76.4095 StartZ=0 EndX=371.073 EndY=76.4095 EndZ=0
    g344: LineSegment StartX=318.073 StartY=72.4095 StartZ=0 EndX=318.073 EndY=-47.4805 EndZ=0
    g345: LineSegment StartX=375.073 StartY=72.4095 StartZ=0 EndX=375.073 EndY=-78.7896 EndZ=0
    g346: ArcOfCircle CenterX=-26.9272 CenterY=22.1087 CenterZ=0 NormalX=0 NormalY=0 NormalZ=1 AngleXU=0 Radius=4 StartAngle=5e-16 EndAngle=3.14159
    g347: LineSegment StartX=-30.9272 StartY=22.1087 StartZ=0 EndX=-34.9272 EndY=-83.7794 EndZ=0
    g348: LineSegment StartX=-18.9272 StartY=-83.7794 StartZ=0 EndX=-22.9272 EndY=22.1087 EndZ=0
  constraints (572):
    c: Coincident(g0,g2)
    c: Block(g0)
    c: Block(g1)
    c: Vertical(g3)
    c: Vertical(g4)
    c: Block(g4)
    c: Block(g3)
    c: Tangent(g6,g7) = 1.5708
    c: Tangent(g7,g9) = 1.5708
    c: Equal(g6,g9)
    c: Coincident(g8,g6)
    c: Coincident(g8,g9)
    c: Block(g7)
    c: Block(g8)
    c: Weight(g10) = 1
    c: Equal(g10,g11)
    c: Equal(g10,g12)
    c: InternalAlignment(g10,g13)
    c: InternalAlignment(g11,g13)
    c: InternalAlignment(g12,g13)
    c: InternalAlignment(g14,g13)
    c: InternalAlignment(g15,g13)
    c: Weight(g16) = 1
    c: Equal(g16,g17)
    c: Equal(g16,g18)
    c: InternalAlignment(g16,g19)
    c: InternalAlignment(g17,g19)
    c: InternalAlignment(g18,g19)
    c: InternalAlignment(g20,g19)
    c: InternalAlignment(g21,g19)
    c: Block(g19)
    c: Block(g13)
    c: Weight(g22) = 1
    c: Equal(g22,g23)
    c: Equal(g22,g24)
    c: InternalAlignment(g22,g25)
    c: InternalAlignment(g23,g25)
    c: InternalAlignment(g24,g25)
    c: InternalAlignment(g26,g25)
    c: InternalAlignment(g27,g25)
    c: Weight(g28) = 1
    c: Equal(g28,g29)
    c: Equal(g28,g30)
    c: InternalAlignment(g28,g31)
    c: InternalAlignment(g29,g31)
    c: InternalAlignment(g30,g31)
    c: InternalAlignment(g32,g31)
    c: InternalAlignment(g33,g31)
    c: Block(g31)
    c: Block(g25)
    c: Weight(g34) = 1
    c: Equal(g34,g35)
    c: Equal(g34,g36)
    c: InternalAlignment(g34,g37)
    c: InternalAlignment(g35,g37)
    c: InternalAlignment(g36,g37)
    c: InternalAlignment(g38,g37)
    c: InternalAlignment(g39,g37)
    c: Weight(g40) = 1
    c: Equal(g40,g41)
    c: Equal(g40,g42)
    c: InternalAlignment(g40,g43)
    c: InternalAlignment(g41,g43)
    c: InternalAlignment(g42,g43)
    c: InternalAlignment(g44,g43)
    c: InternalAlignment(g45,g43)
    c: Block(g37)
    c: Block(g43)
    c: Coincident(g46,g4)
    c: Coincident(g46,g3)
    c: Horizontal(g46)
    c: Distance(g46) = 450
    c: Coincident(g47,g4)
    c: Coincident(g47,g3)
    c: Horizontal(g47)
    c: Horizontal(g48)
    c: Coincident(g2,g48)
    c: Block(g48)
    c: Coincident(g1,g48)
    c: Weight(g49) = 1
    c: Equal(g49,g50)
    c: Equal(g49,g51)
    c: InternalAlignment(g49,g52)
    c: InternalAlignment(g50,g52)
    c: InternalAlignment(g51,g52)
    c: InternalAlignment(g53,g52)
    c: InternalAlignment(g54,g52)
    c: Block(g52)
    c: Weight(g55) = 1
    c: Equal(g55,g56)
    c: Equal(g55,g57)
    c: InternalAlignment(g55,g58)
    c: InternalAlignment(g56,g58)
    c: InternalAlignment(g57,g58)
    c: InternalAlignment(g59,g58)
    c: InternalAlignment(g60,g58)
    c: Block(g58)
    c: Weight(g61) = 1
    c: Equal(g61,g62)
    c: Equal(g61,g63)
    c: InternalAlignment(g61,g64)
    c: InternalAlignment(g62,g64)
    c: InternalAlignment(g63,g64)
    c: InternalAlignment(g65,g64)
    c: InternalAlignment(g66,g64)
    c: Block(g64)
    c: Weight(g67) = 1
    c: Equal(g67,g68)
    c: Equal(g67,g69)
    c: InternalAlignment(g67,g70)
    c: InternalAlignment(g68,g70)
    c: InternalAlignment(g69,g70)
    c: InternalAlignment(g71,g70)
    c: InternalAlignment(g72,g70)
    c: Block(g70)
    c: Weight(g73) = 1
    c: Equal(g73,g74)
    c: Equal(g73,g75)
    c: InternalAlignment(g73,g76)
    c: InternalAlignment(g74,g76)
    c: InternalAlignment(g75,g76)
    c: InternalAlignment(g77,g76)
    c: InternalAlignment(g78,g76)
    c: Weight(g79) = 1
    c: Equal(g79,g80)
    c: Equal(g79,g81)
    c: InternalAlignment(g79,g82)
    c: InternalAlignment(g80,g82)
    c: InternalAlignment(g81,g82)
    c: InternalAlignment(g83,g82)
    c: InternalAlignment(g84,g82)
    c: Block(g76)
    c: Block(g82)
    c: Coincident(g85,g76)
    c: Coincident(g85,g82)
    c: Vertical(g85)
    c: Coincident(g86,g76)
    c: Coincident(g86,g58)
    c: Coincident(g87,g58)
    c: Coincident(g87,g82)
    c: Weight(g88) = 1
    c: Equal(g88,g89)
    c: Equal(g88,g90)
    c: InternalAlignment(g88,g91)
    c: InternalAlignment(g89,g91)
    c: InternalAlignment(g90,g91)
    c: InternalAlignment(g92,g91)
    c: InternalAlignment(g93,g91)
    c: Weight(g94) = 1
    c: Equal(g94,g95)
    c: Equal(g94,g96)
    c: InternalAlignment(g94,g97)
    c: InternalAlignment(g95,g97)
    c: InternalAlignment(g96,g97)
    c: InternalAlignment(g98,g97)
    c: InternalAlignment(g99,g97)
    c: Block(g91)
    c: Block(g97)
    c: Coincident(g100,g91)
    c: Coincident(g100,g97)
    c: Vertical(g100)
    c: Coincident(g101,g91)
    c: Coincident(g101,g52)
    c: Coincident(g102,g52)
    c: Coincident(g102,g97)
    c: Weight(g103) = 1
    c: Equal(g103,g104)
    c: Equal(g103,g105)
    c: InternalAlignment(g103,g106)
    c: InternalAlignment(g104,g106)
    c: InternalAlignment(g105,g106)
    c: InternalAlignment(g107,g106)
    c: InternalAlignment(g108,g106)
    c: Weight(g109) = 1
    c: Equal(g109,g110)
    c: Equal(g109,g111)
    c: InternalAlignment(g109,g112)
    c: InternalAlignment(g110,g112)
    c: InternalAlignment(g111,g112)
    c: InternalAlignment(g113,g112)
    c: InternalAlignment(g114,g112)
    c: Block(g106)
    c: Block(g112)
    c: Coincident(g115,g106)
    c: Coincident(g115,g112)
    c: Vertical(g115)
    c: Coincident(g116,g112)
    c: Coincident(g116,g70)
    c: Coincident(g117,g70)
    c: Coincident(g117,g106)
    c: Weight(g118) = 1
    c: Equal(g118,g119)
    c: Equal(g118,g120)
    c: InternalAlignment(g118,g121)
    c: InternalAlignment(g119,g121)
    c: InternalAlignment(g120,g121)
    c: InternalAlignment(g122,g121)
    c: InternalAlignment(g123,g121)
    c: Weight(g124) = 1
    c: Equal(g124,g125)
    c: Equal(g124,g126)
    c: InternalAlignment(g124,g127)
    c: InternalAlignment(g125,g127)
    c: InternalAlignment(g126,g127)
    c: InternalAlignment(g128,g127)
    c: InternalAlignment(g129,g127)
    c: Block(g121)
    c: Block(g127)
    c: Coincident(g130,g121)
    c: Coincident(g130,g127)
    c: Vertical(g130)
    c: Coincident(g131,g127)
    c: Coincident(g131,g64)
    c: Coincident(g132,g64)
    c: Coincident(g132,g121)
    c: Weight(g133) = 1
    c: Equal(g133,g134)
    c: Equal(g133,g135)
    c: InternalAlignment(g133,g136)
    c: InternalAlignment(g134,g136)
    c: InternalAlignment(g135,g136)
    c: InternalAlignment(g137,g136)
    c: InternalAlignment(g138,g136)
    c: Weight(g139) = 1
    c: Equal(g139,g140)
    c: Equal(g139,g141)
    c: InternalAlignment(g139,g142)
    c: InternalAlignment(g140,g142)
    c: InternalAlignment(g141,g142)
    c: InternalAlignment(g143,g142)
    c: InternalAlignment(g144,g142)
    c: Weight(g145) = 1
    c: Equal(g145,g146)
    c: Equal(g145,g147)
    c: InternalAlignment(g145,g148)
    c: InternalAlignment(g146,g148)
    c: InternalAlignment(g147,g148)
    c: InternalAlignment(g149,g148)
    c: InternalAlignment(g150,g148)
    c: Weight(g151) = 1
    c: Equal(g151,g152)
    c: Equal(g151,g153)
    c: InternalAlignment(g151,g154)
    c: InternalAlignment(g152,g154)
    c: InternalAlignment(g153,g154)
    c: InternalAlignment(g155,g154)
    c: InternalAlignment(g156,g154)
    c: Block(g154)
    c: Block(g148)
    c: Block(g142)
    c: Block(g136)
    c: Coincident(g157,g31)
    c: Coincident(g157,g154)
    c: Coincident(g158,g154)
    c: Coincident(g158,g148)
    c: Horizontal(g158)
    c: Coincident(g159,g148)
    c: Coincident(g159,g31)
    c: Vertical(g159)
    c: Coincident(g160,g25)
    c: Coincident(g160,g142)
    c: Vertical(g160)
    c: Coincident(g161,g142)
    c: Coincident(g161,g136)
    c: Horizontal(g161)
    c: Coincident(g162,g136)
    c: Coincident(g162,g25)
    c: Weight(g163) = 1
    c: Equal(g163,g164)
    c: Equal(g163,g165)
    c: InternalAlignment(g163,g166)
    c: InternalAlignment(g164,g166)
    c: InternalAlignment(g165,g166)
    c: InternalAlignment(g167,g166)
    c: InternalAlignment(g168,g166)
    c: Weight(g169) = 1
    c: Equal(g169,g170)
    c: Equal(g169,g171)
    c: InternalAlignment(g169,g172)
    c: InternalAlignment(g170,g172)
    c: InternalAlignment(g171,g172)
    c: InternalAlignment(g173,g172)
    c: InternalAlignment(g174,g172)
    c: Weight(g175) = 1
    c: Equal(g175,g176)
    c: Equal(g175,g177)
    c: InternalAlignment(g175,g178)
    c: InternalAlignment(g176,g178)
    c: InternalAlignment(g177,g178)
    c: InternalAlignment(g179,g178)
    c: InternalAlignment(g180,g178)
    c: Weight(g181) = 1
    c: Equal(g181,g182)
    c: Equal(g181,g183)
    c: InternalAlignment(g181,g184)
    c: InternalAlignment(g182,g184)
    c: InternalAlignment(g183,g184)
    c: InternalAlignment(g185,g184)
    c: InternalAlignment(g186,g184)
    c: Block(g184)
    c: Block(g178)
    c: Block(g172)
    c: Block(g166)
    c: Coincident(g187,g184)
    c: Coincident(g187,g178)
    c: Horizontal(g187)
    c: Coincident(g188,g178)
    c: Coincident(g188,g13)
    c: Vertical(g188)
    c: Coincident(g189,g19)
    c: Coincident(g189,g172)
    c: Vertical(g189)
    c: Coincident(g190,g172)
    c: Coincident(g190,g166)
    c: Horizontal(g190)
    c: Coincident(g191,g166)
    c: Coincident(g191,g19)
    c: Coincident(g192,g13)
    c: Weight(g193) = 1
    c: Equal(g193,g194)
    c: Equal(g193,g195)
    c: InternalAlignment(g193,g196)
    c: InternalAlignment(g194,g196)
    c: InternalAlignment(g195,g196)
    c: InternalAlignment(g197,g196)
    c: InternalAlignment(g198,g196)
    c: Weight(g199) = 1
    c: Equal(g199,g200)
    c: Equal(g199,g201)
    c: InternalAlignment(g199,g202)
    c: InternalAlignment(g200,g202)
    c: InternalAlignment(g201,g202)
    c: InternalAlignment(g203,g202)
    c: InternalAlignment(g204,g202)
    c: Block(g202)
    c: Block(g196)
    c: Coincident(g205,g202)
    c: Coincident(g205,g37)
    c: Coincident(g206,g37)
    c: Coincident(g206,g196)
    c: Coincident(g207,g196)
    c: Coincident(g207,g202)
    c: Vertical(g207)
    c: Weight(g208) = 1
    c: Equal(g208,g209)
    c: Equal(g208,g210)
    c: InternalAlignment(g208,g211)
    c: InternalAlignment(g209,g211)
    c: InternalAlignment(g210,g211)
    c: InternalAlignment(g212,g211)
    c: InternalAlignment(g213,g211)
    c: Weight(g214) = 1
    c: Equal(g214,g215)
    c: Equal(g214,g216)
    c: InternalAlignment(g214,g217)
    c: InternalAlignment(g215,g217)
    c: InternalAlignment(g216,g217)
    c: InternalAlignment(g218,g217)
    c: InternalAlignment(g219,g217)
    c: Block(g217)
    c: Block(g211)
    c: Coincident(g220,g211)
    c: Coincident(g220,g43)
    c: Coincident(g221,g43)
    c: Coincident(g221,g217)
    c: Coincident(g222,g217)
    c: Coincident(g222,g211)
    c: Vertical(g222)
    c: Horizontal(g223)
    c: Block(g223)
    c: Vertical(g224)
    c: Block(g224)
    c: Block(g225)
    c: Weight(g226) = 1
    c: Equal(g226,g227)
    c: Equal(g226,g228)
    c: InternalAlignment(g226,g229)
    c: InternalAlignment(g227,g229)
    c: InternalAlignment(g228,g229)
    c: InternalAlignment(g230,g229)
    c: InternalAlignment(g231,g229)
    c: Weight(g232) = 1
    c: Equal(g232,g233)
    c: Equal(g232,g234)
    c: InternalAlignment(g232,g235)
    c: InternalAlignment(g233,g235)
    c: InternalAlignment(g234,g235)
    c: InternalAlignment(g236,g235)
    c: InternalAlignment(g237,g235)
    c: Weight(g238) = 1
    c: Equal(g238,g239)
    c: Equal(g238,g240)
    c: InternalAlignment(g238,g241)
    c: InternalAlignment(g239,g241)
    c: InternalAlignment(g240,g241)
    c: InternalAlignment(g242,g241)
    c: InternalAlignment(g243,g241)
    c: Weight(g244) = 1
    c: Equal(g244,g245)
    c: Equal(g244,g246)
    c: InternalAlignment(g244,g247)
    c: InternalAlignment(g245,g247)
    c: InternalAlignment(g246,g247)
    c: InternalAlignment(g248,g247)
    c: InternalAlignment(g249,g247)
    c: Block(g229)
    c: Block(g235)
    c: Block(g241)
    c: Block(g247)
    c: Coincident(g250,g235)
    c: Coincident(g250,g229)
    c: Horizontal(g250)
    c: Block(g192)
    c: Weight(g251) = 1
    c: Equal(g251,g252)
    c: Equal(g251,g253)
    c: InternalAlignment(g251,g254)
    c: InternalAlignment(g252,g254)
    c: InternalAlignment(g253,g254)
    c: InternalAlignment(g255,g254)
    c: InternalAlignment(g256,g254)
    c: Weight(g257) = 1
    c: Equal(g257,g258)
    c: Equal(g257,g259)
    c: InternalAlignment(g257,g260)
    c: InternalAlignment(g258,g260)
    c: InternalAlignment(g259,g260)
    c: InternalAlignment(g261,g260)
    c: InternalAlignment(g262,g260)
    c: Block(g254)
    c: Block(g260)
    c: Coincident(g263,g254)
    c: Coincident(g263,g260)
    c: Weight(g264) = 1
    c: Equal(g264,g265)
    c: Equal(g264,g266)
    c: InternalAlignment(g264,g267)
    c: InternalAlignment(g265,g267)
    c: InternalAlignment(g266,g267)
    c: InternalAlignment(g268,g267)
    c: InternalAlignment(g269,g267)
    c: Weight(g270) = 1
    c: Equal(g270,g271)
    c: Equal(g270,g272)
    c: InternalAlignment(g270,g273)
    c: InternalAlignment(g271,g273)
    c: InternalAlignment(g272,g273)
    c: InternalAlignment(g274,g273)
    c: InternalAlignment(g275,g273)
    c: Weight(g276) = 1
    c: Equal(g276,g277)
    c: Equal(g276,g278)
    c: InternalAlignment(g276,g279)
    c: InternalAlignment(g277,g279)
    c: InternalAlignment(g278,g279)
    c: InternalAlignment(g280,g279)
    c: InternalAlignment(g281,g279)
    c: Block(g279)
    c: Block(g273)
    c: Block(g267)
    c: Coincident(g282,g273)
    c: Coincident(g282,g267)
    c: Coincident(g283,g267)
    c: Coincident(g283,g279)
    c: Vertical(g283)
    c: Coincident(g284,g279)
    c: Coincident(g284,g273)
    c: Horizontal(g284)
    c: Weight(g285) = 1
    c: Equal(g285,g286)
    c: InternalAlignment(g285,g287)
    c: InternalAlignment(g286,g287)
    c: InternalAlignment(g288,g287)
    c: InternalAlignment(g289,g287)
    c: Weight(g290) = 1
    c: InternalAlignment(g291,g293)
    c: InternalAlignment(g292,g293)
    c: InternalAlignment(g294,g293)
    c: InternalAlignment(g295,g293)
    c: Weight(g296) = 1
    c: Equal(g296,g297)
    c: Equal(g296,g298)
    c: InternalAlignment(g296,g299)
    c: InternalAlignment(g297,g299)
    c: InternalAlignment(g298,g299)
    c: InternalAlignment(g300,g299)
    c: InternalAlignment(g301,g299)
    c: Equal(g302,g303)
    c: Equal(g302,g304)
    c: InternalAlignment(g302,g305)
    c: InternalAlignment(g303,g305)
    c: InternalAlignment(g304,g305)
    c: InternalAlignment(g306,g305)
    c: InternalAlignment(g307,g305)
    c: Block(g293)
    c: Block(g299)
    c: Block(g305)
    c: Block(g287)
    c: Coincident(g308,g287)
    c: Coincident(g308,g293)
    c: Horizontal(g308)
    c: Coincident(g309,g293)
    c: Coincident(g309,g299)
    c: Vertical(g309)
    c: Coincident(g310,g299)
    c: Coincident(g310,g305)
    c: Horizontal(g310)
    c: Coincident(g311,g305)
    c: Coincident(g311,g287)
    c: Weight(g312) = 1
    c: Equal(g312,g313)
    c: Equal(g312,g314)
    c: InternalAlignment(g312,g315)
    c: InternalAlignment(g313,g315)
    c: InternalAlignment(g314,g315)
    c: InternalAlignment(g316,g315)
    c: InternalAlignment(g317,g315)
    c: Weight(g318) = 1
    c: Equal(g318,g319)
    c: Equal(g318,g320)
    c: InternalAlignment(g318,g321)
    c: InternalAlignment(g319,g321)
    c: InternalAlignment(g320,g321)
    c: InternalAlignment(g322,g321)
    c: InternalAlignment(g323,g321)
    c: Weight(g324) = 1
    c: Equal(g324,g325)
    c: Equal(g324,g326)
    c: InternalAlignment(g324,g327)
    c: InternalAlignment(g325,g327)
    c: InternalAlignment(g326,g327)
    c: InternalAlignment(g328,g327)
    c: InternalAlignment(g329,g327)
    c: Block(g327)
    c: Block(g321)
    c: Block(g315)
    c: Coincident(g330,g327)
    c: Coincident(g330,g321)
    c: Horizontal(g330)
    c: Coincident(g331,g321)
    c: Coincident(g331,g315)
    c: Vertical(g331)
    c: Coincident(g332,g315)
    c: Coincident(g332,g327)
    c: InternalAlignment(g333,g334)
    c: InternalAlignment(g335,g334)
    c: InternalAlignment(g336,g334)
    c: Block(g334)
    c: Equal(g337,g338)
    c: Equal(g337,g339)
    c: InternalAlignment(g337,g340)
    c: InternalAlignment(g338,g340)
    c: InternalAlignment(g339,g340)
    c: InternalAlignment(g341,g340)
    c: InternalAlignment(g342,g340)
    c: Block(g340)
    c: Coincident(g343,g334)
    c: Horizontal(g343)
    c: Block(g343)
    c: Coincident(g344,g334)
    c: Coincident(g344,g260)
    c: Vertical(g344)
    c: Coincident(g345,g340)
    c: Coincident(g345,g254)
    c: Vertical(g345)
    c: Coincident(g347,g5)
    c: Coincident(g348,g5)
    c: Block(g346)
    c: Block(g5)
    c: Block(g348)
    c: Block(g347)
    c: Distance(g344) = 119.89
FEATURE [Sketcher::SketchObject] Sketch001
  FullyConstrained = true
  MapMode = 4
  Placement = pos=(0,0,0) rot=(0.57735,0.57735,0.57735;2.0944rad)
  Support = -> [Sketch]
  sketch-geometry (46):
    g0: BSplineCurve PolesCount=3 KnotsCount=2 Degree=2 IsPeriodic=0
    g1: ArcOfCircle CenterX=73.1223 CenterY=-32.291 CenterZ=0 NormalX=0 NormalY=0 NormalZ=1 AngleXU=0 Radius=13 StartAngle=5.92268 EndAngle=9.06428
    g2: ArcOfCircle CenterX=66.7816 CenterY=-49.1439 CenterZ=0 NormalX=0 NormalY=0 NormalZ=1 AngleXU=0 Radius=13 StartAngle=2.78068 EndAngle=5.92131
    g3: ArcOfCircle CenterX=55.9263 CenterY=-78.1807 CenterZ=0 NormalX=0 NormalY=0 NormalZ=1 AngleXU=0 Radius=13 StartAngle=5.92268 EndAngle=9.06428
    g4: ArcOfCircle CenterX=49.5884 CenterY=-95.0342 CenterZ=0 NormalX=0 NormalY=0 NormalZ=1 AngleXU=0 Radius=13 StartAngle=2.78068 EndAngle=5.92131
    g5: ArcOfCircle CenterX=38.7206 CenterY=-124.067 CenterZ=0 NormalX=0 NormalY=0 NormalZ=1 AngleXU=0 Radius=13 StartAngle=5.92268 EndAngle=9.06428
    g6: ArcOfCircle CenterX=32.3875 CenterY=-140.92 CenterZ=0 NormalX=0 NormalY=0 NormalZ=1 AngleXU=0 Radius=13 StartAngle=2.78068 EndAngle=5.92131
    g7: ArcOfCircle CenterX=21.4715 CenterY=-169.934 CenterZ=0 NormalX=0 NormalY=0 NormalZ=1 AngleXU=0 Radius=13 StartAngle=5.92268 EndAngle=9.06428
    g8: ArcOfCircle CenterX=15.1336 CenterY=-186.787 CenterZ=0 NormalX=0 NormalY=0 NormalZ=1 AngleXU=0 Radius=13 StartAngle=2.78068 EndAngle=5.92131
    g9-g12: Circle x4 (B-spline internal-alignment scaffolding for g13; pole/knot coordinates omitted)
    g13: BSplineCurve PolesCount=4 KnotsCount=2 Degree=3 IsPeriodic=0
    g14: GeomPoint X=28.8094 Y=-19.0875 Z=0
    g15: GeomPoint X=47.0443 Y=-50.4712 Z=0
    g16: Circle CenterX=53.5586 CenterY=-23.2695 CenterZ=0 NormalX=0 NormalY=0 NormalZ=1 AngleXU=0 Radius=3.24518
    g17: Circle CenterX=-195.441 CenterY=-127.082 CenterZ=0 NormalX=0 NormalY=0 NormalZ=1 AngleXU=0 Radius=1
    g18: Circle CenterX=-8.24091 CenterY=-197.481 CenterZ=0 NormalX=0 NormalY=0 NormalZ=1 AngleXU=0 Radius=1
    g19: Circle CenterX=12.8789 CenterY=-141.321 CenterZ=0 NormalX=0 NormalY=0 NormalZ=1 AngleXU=0 Radius=1
    g20: BSplineCurve PolesCount=3 KnotsCount=2 Degree=2 IsPeriodic=0
    g21: GeomPoint X=-195.441 Y=-127.082 Z=0
    g22: GeomPoint X=12.8789 Y=-141.321 Z=0
    g23: Circle CenterX=-12.8016 CenterY=-179.036 CenterZ=0 NormalX=0 NormalY=0 NormalZ=1 AngleXU=0 Radius=10.5072
    g24: Circle CenterX=0.933922 CenterY=-166.43 CenterZ=0 NormalX=0 NormalY=0 NormalZ=1 AngleXU=0 Radius=3.26661
    g25: Circle CenterX=-33.5518 CenterY=-176.44 CenterZ=0 NormalX=0 NormalY=0 NormalZ=1 AngleXU=0 Radius=5.64388
    g26: Circle CenterX=-47.2366 CenterY=-173.859 CenterZ=0 NormalX=0 NormalY=0 NormalZ=1 AngleXU=0 Radius=3.01653
    g27: Circle CenterX=-56.2595 CenterY=-171.456 CenterZ=0 NormalX=0 NormalY=0 NormalZ=1 AngleXU=0 Radius=2.12826
    g28: ArcOfCircle CenterX=51.2151 CenterY=-198.473 CenterZ=0 NormalX=0 NormalY=0 NormalZ=1 AngleXU=0 Radius=20 StartAngle=2.78189 EndAngle=4.35269
    g29: LineSegment StartX=32.4951 StartY=-191.433 StartZ=0 EndX=94.6578 EndY=-26.1352 EndZ=0
    g30: LineSegment StartX=43.1192 StartY=-220.001 StartZ=0 EndX=-196.497 EndY=-129.89 EndZ=0
    g31: LineSegment StartX=43.1192 StartY=-220.001 StartZ=0 EndX=44.1752 EndY=-217.193 EndZ=0
    g32: LineSegment StartX=117.223 StartY=-19.0875 StartZ=0 EndX=117.223 EndY=-16.0875 EndZ=0
    g33: LineSegment StartX=117.223 StartY=-16.0875 StartZ=0 EndX=17.2232 EndY=-16.0875 EndZ=0
    g34: LineSegment StartX=17.2232 StartY=-16.0875 StartZ=0 EndX=17.2232 EndY=-19.0875 EndZ=0
    g35: LineSegment StartX=28.8094 StartY=-19.0875 StartZ=0 EndX=17.2232 EndY=-19.0875 EndZ=0
    g36: LineSegment StartX=47.0443 StartY=-50.4712 StartZ=0 EndX=12.8789 EndY=-141.321 EndZ=0
    g37: LineSegment StartX=-195.441 StartY=-127.082 StartZ=0 EndX=-196.497 EndY=-129.89 EndZ=0
    g38: LineSegment StartX=85.2866 StartY=-36.8766 StartZ=0 EndX=78.9396 EndY=-53.7463 EndZ=0
    g39: LineSegment StartX=60.9579 StartY=-27.7053 StartZ=0 EndX=54.6191 EndY=-44.5532 EndZ=0
    g40: LineSegment StartX=68.0907 StartY=-82.7664 StartZ=0 EndX=61.7465 EndY=-99.6365 EndZ=0
    g41: LineSegment StartX=43.7619 StartY=-73.595 StartZ=0 EndX=37.426 EndY=-90.4435 EndZ=0
    g42: LineSegment StartX=50.885 StartY=-128.652 StartZ=0 EndX=44.5456 EndY=-145.522 EndZ=0
    g43: LineSegment StartX=26.5562 StartY=-119.481 StartZ=0 EndX=20.2251 EndY=-136.329 EndZ=0
    g44: LineSegment StartX=9.3071 StartY=-165.349 StartZ=0 EndX=2.97115 EndY=-182.197 EndZ=0
    g45: LineSegment StartX=33.6358 StartY=-174.52 StartZ=0 EndX=27.2917 EndY=-191.39 EndZ=0
  constraints (71):
    c: Block(g0)
    c: Block(g1)
    c: Block(g2)
    c: Block(g4)
    c: Block(g3)
    c: Block(g6)
    c: Block(g5)
    c: Block(g8)
    c: Block(g7)
    c: Weight(g9) = 1
    c: Equal(g9,g10)
    c: Equal(g9,g11)
    c: Equal(g9,g12)
    c: InternalAlignment(g9-g12 -> g13) x4
    c: InternalAlignment(g14,g13)
    c: InternalAlignment(g15,g13)
    c: Block(g16)
    c: Weight(g17) = 1
    c: Equal(g17,g18)
    c: Equal(g17,g19)
    c: InternalAlignment(g17,g20)
    c: InternalAlignment(g18,g20)
    c: InternalAlignment(g19,g20)
    c: InternalAlignment(g21,g20)
    c: InternalAlignment(g22,g20)
    c: Block(g20)
    c: Block(g23)
    c: Block(g24)
    c: Block(g25)
    c: Block(g26)
    c: Block(g27)
    c: Block(g28)
    c: Coincident(g29,g28)
    c: Coincident(g29,g0)
    c: Block(g13)
    c: Coincident(g31,g30)
    c: Coincident(g31,g28)
    c: Block(g31)
    c: Coincident(g32,g0)
    c: Vertical(g32)
    c: Coincident(g33,g32)
    c: Horizontal(g33)
    c: Coincident(g34,g33)
    c: Vertical(g34)
    c: Block(g33)
    c: Coincident(g35,g13)
    c: Coincident(g35,g34)
    c: Horizontal(g35)
    c: Coincident(g36,g13)
    c: Coincident(g36,g20)
    c: Coincident(g37,g20)
    c: Coincident(g37,g30)
    c: Block(g30)
    c: Coincident(g38,g1)
    c: Coincident(g38,g2)
    c: Coincident(g39,g1)
    c: Coincident(g39,g2)
    c: Coincident(g40,g3)
    c: Coincident(g40,g4)
    c: Coincident(g41,g3)
    c: Coincident(g41,g4)
    c: Coincident(g42,g5)
    c: Coincident(g42,g6)
    c: Coincident(g43,g5)
    c: Coincident(g43,g6)
    c: Coincident(g44,g7)
    c: Coincident(g44,g8)
    c: Coincident(g45,g7)
    c: Coincident(g45,g8)
    c: Distance(g30) = 256
    c: Distance(g33) = 100
FEATURE [Part::Extrusion] Extrude002
  Base = -> Sketch001
  Dir = (1,0,0)
  DirMode = 2
  FaceMakerClass = Part::FaceMakerBullseye
  LengthFwd = 8
  LengthRev = 0
  Solid = true
  Symmetric = false
FEATURE [Sketcher::SketchObject] Sketch002
  FullyConstrained = true
  sketch-geometry (20):
    g0: LineSegment StartX=-2.77179 StartY=-200.304 StartZ=0 EndX=5.22821 EndY=-200.304 EndZ=0
    g1: LineSegment StartX=5.22821 StartY=-200.304 StartZ=0 EndX=5.22821 EndY=-197.304 EndZ=0
    g2: LineSegment StartX=-2.77179 StartY=-200.304 StartZ=0 EndX=-2.77179 EndY=-197.304 EndZ=0
    g3: LineSegment StartX=5.22821 StartY=-197.304 StartZ=0 EndX=8.22821 EndY=-197.304 EndZ=0
    g4: LineSegment StartX=-2.77179 StartY=-197.304 StartZ=0 EndX=-5.77179 EndY=-197.304 EndZ=0
    g5: LineSegment StartX=19.2282 StartY=-203.304 StartZ=0 EndX=19.2282 EndY=-206.304 EndZ=0
    g6: LineSegment StartX=-16.7718 StartY=-203.304 StartZ=0 EndX=-16.7718 EndY=-206.304 EndZ=0
    g7: LineSegment StartX=-16.7718 StartY=-206.304 StartZ=0 EndX=19.2282 EndY=-206.304 EndZ=0
    g8: Circle CenterX=-16.7718 CenterY=-203.304 CenterZ=0 NormalX=0 NormalY=0 NormalZ=1 AngleXU=0 Radius=1
    g9: Circle CenterX=-5.77179 CenterY=-203.304 CenterZ=0 NormalX=0 NormalY=0 NormalZ=1 AngleXU=0 Radius=1
    g10: Circle CenterX=-5.77179 CenterY=-197.304 CenterZ=0 NormalX=0 NormalY=0 NormalZ=1 AngleXU=0 Radius=1
    g11: BSplineCurve PolesCount=3 KnotsCount=2 Degree=2 IsPeriodic=0
    g12: GeomPoint X=-16.7718 Y=-203.304 Z=0
    g13: GeomPoint X=-5.77179 Y=-197.304 Z=0
    g14: Circle CenterX=19.2282 CenterY=-203.304 CenterZ=0 NormalX=0 NormalY=0 NormalZ=1 AngleXU=0 Radius=1
    g15: Circle CenterX=8.22821 CenterY=-203.304 CenterZ=0 NormalX=0 NormalY=0 NormalZ=1 AngleXU=0 Radius=1
    g16: Circle CenterX=8.22821 CenterY=-197.304 CenterZ=0 NormalX=0 NormalY=0 NormalZ=1 AngleXU=0 Radius=1
    g17: BSplineCurve PolesCount=3 KnotsCount=2 Degree=2 IsPeriodic=0
    g18: GeomPoint X=19.2282 Y=-203.304 Z=0
    g19: GeomPoint X=8.22821 Y=-197.304 Z=0
  constraints (41):
    c: Horizontal(g0)
    c: Distance(g0) = 8
    c: Coincident(g1,g0)
    c: Vertical(g1)
    c: Distance(g1) = 3
    c: Coincident(g2,g0)
    c: Vertical(g2)
    c: Distance(g2) = 3
    c: Coincident(g3,g1)
    c: Horizontal(g3)
    c: Distance(g3) = 3
    c: Coincident(g4,g2)
    c: Horizontal(g4)
    c: Distance(g4) = 3
    c: Vertical(g5)
    c: Vertical(g6)
    c: Coincident(g7,g6)
    c: Coincident(g7,g5)
    c: Weight(g8) = 1
    c: Equal(g8,g9)
    c: Equal(g8,g10)
    c: Coincident(g11,g4)
    c: InternalAlignment(g8,g11)
    c: InternalAlignment(g9,g11)
    c: InternalAlignment(g10,g11)
    c: InternalAlignment(g12,g11)
    c: InternalAlignment(g13,g11)
    c: Coincident(g17,g5)
    c: Weight(g14) = 1
    c: Equal(g14,g15)
    c: Equal(g14,g16)
    c: Coincident(g17,g3)
    c: InternalAlignment(g14,g17)
    c: InternalAlignment(g15,g17)
    c: InternalAlignment(g16,g17)
    c: InternalAlignment(g18,g17)
    c: InternalAlignment(g19,g17)
    c: Block(g7)
    c: Block(g17)
    c: Block(g11)
    c: Block(g6)
FEATURE [Part::Extrusion] Extrude003
  Base = -> Sketch002
  Dir = (0,0,1)
  DirMode = 2
  FaceMakerClass = Part::FaceMakerBullseye
  LengthFwd = 260
  LengthRev = 0
  Solid = true
  Symmetric = false
FEATURE [Sketcher::SketchObject] Sketch003
  FullyConstrained = false
  sketch-geometry (425):
    g0: LineSegment StartX=-42.9272 StartY=136.221 StartZ=0 EndX=-42.9272 EndY=-103.779 EndZ=0
    g1: LineSegment StartX=407.073 StartY=136.221 StartZ=0 EndX=407.073 EndY=-103.779 EndZ=0
    g2: ArcOfCircle CenterX=-26.9272 CenterY=-83.7794 CenterZ=0 NormalX=0 NormalY=0 NormalZ=1 AngleXU=0 Radius=8 StartAngle=3.14159 EndAngle=6.28319
    g3: ArcOfCircle CenterX=391.073 CenterY=-83.7794 CenterZ=0 NormalX=0 NormalY=0 NormalZ=1 AngleXU=0 Radius=8 StartAngle=3.14159 EndAngle=6.28319
    g4: Circle CenterX=175.022 CenterY=27.0628 CenterZ=0 NormalX=0 NormalY=0 NormalZ=1 AngleXU=0 Radius=1
    g5: Circle CenterX=179.022 CenterY=24.8665 CenterZ=0 NormalX=0 NormalY=0 NormalZ=1 AngleXU=0 Radius=1
    g6: Circle CenterX=179.022 CenterY=27.0628 CenterZ=0 NormalX=0 NormalY=0 NormalZ=1 AngleXU=0 Radius=1
    g7: BSplineCurve PolesCount=3 KnotsCount=2 Degree=2 IsPeriodic=0
    g8: GeomPoint X=175.022 Y=27.0628 Z=0
    g9: GeomPoint X=179.022 Y=27.0628 Z=0
    g10: Circle CenterX=189.124 CenterY=27.0628 CenterZ=0 NormalX=0 NormalY=0 NormalZ=1 AngleXU=0 Radius=1
    g11: Circle CenterX=185.124 CenterY=24.8665 CenterZ=0 NormalX=0 NormalY=0 NormalZ=1 AngleXU=0 Radius=1
    g12: Circle CenterX=185.124 CenterY=27.0628 CenterZ=0 NormalX=0 NormalY=0 NormalZ=1 AngleXU=0 Radius=1
    g13: BSplineCurve PolesCount=3 KnotsCount=2 Degree=2 IsPeriodic=0
    g14: GeomPoint X=189.124 Y=27.0628 Z=0
    g15: GeomPoint X=185.124 Y=27.0628 Z=0
    g16: Circle CenterX=175.022 CenterY=5.37834 CenterZ=0 NormalX=0 NormalY=0 NormalZ=1 AngleXU=0 Radius=1
    g17: Circle CenterX=179.022 CenterY=7.57463 CenterZ=0 NormalX=0 NormalY=0 NormalZ=1 AngleXU=0 Radius=1
    g18: Circle CenterX=179.022 CenterY=5.34704 CenterZ=0 NormalX=0 NormalY=0 NormalZ=1 AngleXU=0 Radius=1
    g19: BSplineCurve PolesCount=3 KnotsCount=2 Degree=2 IsPeriodic=0
    g20: GeomPoint X=175.022 Y=5.37834 Z=0
    g21: GeomPoint X=179.022 Y=5.34704 Z=0
    g22: Circle CenterX=189.124 CenterY=5.37834 CenterZ=0 NormalX=0 NormalY=0 NormalZ=1 AngleXU=0 Radius=1
    g23: Circle CenterX=185.124 CenterY=7.57463 CenterZ=0 NormalX=0 NormalY=0 NormalZ=1 AngleXU=0 Radius=1
    g24: Circle CenterX=185.124 CenterY=5.34704 CenterZ=0 NormalX=0 NormalY=0 NormalZ=1 AngleXU=0 Radius=1
    g25: BSplineCurve PolesCount=3 KnotsCount=2 Degree=2 IsPeriodic=0
    g26: GeomPoint X=189.124 Y=5.37834 Z=0
    g27: GeomPoint X=185.124 Y=5.34704 Z=0
    g28: Circle CenterX=165.871 CenterY=18.1458 CenterZ=0 NormalX=0 NormalY=0 NormalZ=1 AngleXU=0 Radius=1
    g29: Circle CenterX=169.377 CenterY=16.2206 CenterZ=0 NormalX=0 NormalY=0 NormalZ=1 AngleXU=0 Radius=1
    g30: Circle CenterX=165.871 CenterY=14.2954 CenterZ=0 NormalX=0 NormalY=0 NormalZ=1 AngleXU=0 Radius=1
    g31: BSplineCurve PolesCount=3 KnotsCount=2 Degree=2 IsPeriodic=0
    g32: GeomPoint X=165.871 Y=18.1458 Z=0
    g33: GeomPoint X=165.871 Y=14.2954 Z=0
    g34: Circle CenterX=198.275 CenterY=18.1458 CenterZ=0 NormalX=0 NormalY=0 NormalZ=1 AngleXU=0 Radius=1
    g35: Circle CenterX=194.768 CenterY=16.2206 CenterZ=0 NormalX=0 NormalY=0 NormalZ=1 AngleXU=0 Radius=1
    g36: Circle CenterX=198.275 CenterY=14.2954 CenterZ=0 NormalX=0 NormalY=0 NormalZ=1 AngleXU=0 Radius=1
    g37: BSplineCurve PolesCount=3 KnotsCount=2 Degree=2 IsPeriodic=0
    g38: GeomPoint X=198.275 Y=18.1458 Z=0
    g39: GeomPoint X=198.275 Y=14.2954 Z=0
    g40: LineSegment StartX=407.073 StartY=-103.779 StartZ=0 EndX=-42.9272 EndY=-103.779 EndZ=0
    g41: Circle CenterX=125.607 CenterY=54.1951 CenterZ=0 NormalX=0 NormalY=0 NormalZ=1 AngleXU=0 Radius=1
    g42: Circle CenterX=139.632 CenterY=46.4944 CenterZ=0 NormalX=0 NormalY=0 NormalZ=1 AngleXU=0 Radius=1
    g43: Circle CenterX=127.326 CenterY=56.7187 CenterZ=0 NormalX=0 NormalY=0 NormalZ=1 AngleXU=0 Radius=1
    g44: BSplineCurve PolesCount=3 KnotsCount=2 Degree=2 IsPeriodic=0
    g45: GeomPoint X=125.607 Y=54.1951 Z=0
    g46: GeomPoint X=127.326 Y=56.7187 Z=0
    g47: Circle CenterX=236.821 CenterY=56.7187 CenterZ=0 NormalX=0 NormalY=0 NormalZ=1 AngleXU=0 Radius=1
    g48: Circle CenterX=224.513 CenterY=46.4944 CenterZ=0 NormalX=0 NormalY=0 NormalZ=1 AngleXU=0 Radius=1
    g49: Circle CenterX=238.538 CenterY=54.1951 CenterZ=0 NormalX=0 NormalY=0 NormalZ=1 AngleXU=0 Radius=1
    g50: BSplineCurve PolesCount=3 KnotsCount=2 Degree=2 IsPeriodic=0
    g51: GeomPoint X=236.821 Y=56.7187 Z=0
    g52: GeomPoint X=238.538 Y=54.1951 Z=0
    g53: Circle CenterX=238.538 CenterY=-21.7539 CenterZ=0 NormalX=0 NormalY=0 NormalZ=1 AngleXU=0 Radius=1
    g54: Circle CenterX=224.513 CenterY=-14.0532 CenterZ=0 NormalX=0 NormalY=0 NormalZ=1 AngleXU=0 Radius=1
    g55: Circle CenterX=236.821 CenterY=-24.2775 CenterZ=0 NormalX=0 NormalY=0 NormalZ=1 AngleXU=0 Radius=1
    g56: BSplineCurve PolesCount=3 KnotsCount=2 Degree=2 IsPeriodic=0
    g57: GeomPoint X=238.538 Y=-21.7539 Z=0
    g58: GeomPoint X=236.821 Y=-24.2775 Z=0
    g59: Circle CenterX=125.607 CenterY=-21.7539 CenterZ=0 NormalX=0 NormalY=0 NormalZ=1 AngleXU=0 Radius=1
    g60: Circle CenterX=139.632 CenterY=-14.0532 CenterZ=0 NormalX=0 NormalY=0 NormalZ=1 AngleXU=0 Radius=1
    g61: Circle CenterX=127.325 CenterY=-24.2775 CenterZ=0 NormalX=0 NormalY=0 NormalZ=1 AngleXU=0 Radius=1
    g62: BSplineCurve PolesCount=3 KnotsCount=2 Degree=2 IsPeriodic=0
    g63: GeomPoint X=125.607 Y=-21.7539 Z=0
    g64: GeomPoint X=127.325 Y=-24.2775 Z=0
    g65: Circle CenterX=302.996 CenterY=111.695 CenterZ=0 NormalX=0 NormalY=0 NormalZ=1 AngleXU=0 Radius=1
    g66: Circle CenterX=306.073 CenterY=114.251 CenterZ=0 NormalX=0 NormalY=0 NormalZ=1 AngleXU=0 Radius=1
    g67: Circle CenterX=306.073 CenterY=110.251 CenterZ=0 NormalX=0 NormalY=0 NormalZ=1 AngleXU=0 Radius=1
    g68: BSplineCurve PolesCount=3 KnotsCount=2 Degree=2 IsPeriodic=0
    g69: GeomPoint X=302.996 Y=111.695 Z=0
    g70: GeomPoint X=306.073 Y=110.251 Z=0
    g71: Circle CenterX=306.073 CenterY=95.2763 CenterZ=0 NormalX=0 NormalY=0 NormalZ=1 AngleXU=0 Radius=1
    g72: Circle CenterX=306.073 CenterY=91.2763 CenterZ=0 NormalX=0 NormalY=0 NormalZ=1 AngleXU=0 Radius=1
    g73: Circle CenterX=302.567 CenterY=89.3511 CenterZ=0 NormalX=0 NormalY=0 NormalZ=1 AngleXU=0 Radius=1
    g74: BSplineCurve PolesCount=3 KnotsCount=2 Degree=2 IsPeriodic=0
    g75: GeomPoint X=306.073 Y=95.2763 Z=0
    g76: GeomPoint X=302.567 Y=89.3511 Z=0
    g77: LineSegment StartX=306.073 StartY=110.251 StartZ=0 EndX=306.073 EndY=95.2763 EndZ=0
    g78: LineSegment StartX=302.996 StartY=111.695 StartZ=0 EndX=236.821 EndY=56.7187 EndZ=0
    g79: LineSegment StartX=238.538 StartY=54.1951 StartZ=0 EndX=302.567 EndY=89.3511 EndZ=0
    g80: Circle CenterX=61.1496 CenterY=111.695 CenterZ=0 NormalX=0 NormalY=0 NormalZ=1 AngleXU=0 Radius=1
    g81: Circle CenterX=58.0728 CenterY=114.251 CenterZ=0 NormalX=0 NormalY=0 NormalZ=1 AngleXU=0 Radius=1
    g82: Circle CenterX=58.0728 CenterY=110.251 CenterZ=0 NormalX=0 NormalY=0 NormalZ=1 AngleXU=0 Radius=1
    g83: BSplineCurve PolesCount=3 KnotsCount=2 Degree=2 IsPeriodic=0
    g84: GeomPoint X=61.1496 Y=111.695 Z=0
    g85: GeomPoint X=58.0728 Y=110.251 Z=0
    g86: Circle CenterX=61.5791 CenterY=89.3511 CenterZ=0 NormalX=0 NormalY=0 NormalZ=1 AngleXU=0 Radius=1
    g87: Circle CenterX=58.0728 CenterY=91.2763 CenterZ=0 NormalX=0 NormalY=0 NormalZ=1 AngleXU=0 Radius=1
    g88: Circle CenterX=58.0728 CenterY=95.2763 CenterZ=0 NormalX=0 NormalY=0 NormalZ=1 AngleXU=0 Radius=1
    g89: BSplineCurve PolesCount=3 KnotsCount=2 Degree=2 IsPeriodic=0
    g90: GeomPoint X=61.5791 Y=89.3511 Z=0
    g91: GeomPoint X=58.0728 Y=95.2763 Z=0
    g92: LineSegment StartX=58.0728 StartY=110.251 StartZ=0 EndX=58.0728 EndY=95.2763 EndZ=0
    g93: LineSegment StartX=61.1496 StartY=111.695 StartZ=0 EndX=127.326 EndY=56.7187 EndZ=0
    g94: LineSegment StartX=125.607 StartY=54.1951 StartZ=0 EndX=61.5791 EndY=89.3511 EndZ=0
    g95: Circle CenterX=61.5791 CenterY=-56.9099 CenterZ=0 NormalX=0 NormalY=0 NormalZ=1 AngleXU=0 Radius=1
    g96: Circle CenterX=58.0728 CenterY=-58.8351 CenterZ=0 NormalX=0 NormalY=0 NormalZ=1 AngleXU=0 Radius=1
    g97: Circle CenterX=58.0728 CenterY=-62.8351 CenterZ=0 NormalX=0 NormalY=0 NormalZ=1 AngleXU=0 Radius=1
    g98: BSplineCurve PolesCount=3 KnotsCount=2 Degree=2 IsPeriodic=0
    g99: GeomPoint X=61.5791 Y=-56.9099 Z=0
    g100: GeomPoint X=58.0728 Y=-62.8351 Z=0
    g101: Circle CenterX=58.0728 CenterY=-77.8102 CenterZ=0 NormalX=0 NormalY=0 NormalZ=1 AngleXU=0 Radius=1
    g102: Circle CenterX=58.0728 CenterY=-81.8102 CenterZ=0 NormalX=0 NormalY=0 NormalZ=1 AngleXU=0 Radius=1
    g103: Circle CenterX=61.1496 CenterY=-79.2541 CenterZ=0 NormalX=0 NormalY=0 NormalZ=1 AngleXU=0 Radius=1
    g104: BSplineCurve PolesCount=3 KnotsCount=2 Degree=2 IsPeriodic=0
    g105: GeomPoint X=58.0728 Y=-77.8102 Z=0
    g106: GeomPoint X=61.1496 Y=-79.2541 Z=0
    g107: LineSegment StartX=58.0728 StartY=-62.8351 StartZ=0 EndX=58.0728 EndY=-77.8102 EndZ=0
    g108: LineSegment StartX=61.1496 StartY=-79.2541 StartZ=0 EndX=127.325 EndY=-24.2775 EndZ=0
    g109: LineSegment StartX=125.607 StartY=-21.7539 StartZ=0 EndX=61.5791 EndY=-56.9099 EndZ=0
    g110: Circle CenterX=302.567 CenterY=-56.9099 CenterZ=0 NormalX=0 NormalY=0 NormalZ=1 AngleXU=0 Radius=1
    g111: Circle CenterX=306.073 CenterY=-58.8351 CenterZ=0 NormalX=0 NormalY=0 NormalZ=1 AngleXU=0 Radius=1
    g112: Circle CenterX=306.073 CenterY=-62.8351 CenterZ=0 NormalX=0 NormalY=0 NormalZ=1 AngleXU=0 Radius=1
    g113: BSplineCurve PolesCount=3 KnotsCount=2 Degree=2 IsPeriodic=0
    g114: GeomPoint X=302.567 Y=-56.9099 Z=0
    g115: GeomPoint X=306.073 Y=-62.8351 Z=0
    g116: Circle CenterX=302.996 CenterY=-79.2541 CenterZ=0 NormalX=0 NormalY=0 NormalZ=1 AngleXU=0 Radius=1
    g117: Circle CenterX=306.073 CenterY=-81.8102 CenterZ=0 NormalX=0 NormalY=0 NormalZ=1 AngleXU=0 Radius=1
    g118: Circle CenterX=306.073 CenterY=-77.8102 CenterZ=0 NormalX=0 NormalY=0 NormalZ=1 AngleXU=0 Radius=1
    g119: BSplineCurve PolesCount=3 KnotsCount=2 Degree=2 IsPeriodic=0
    g120: GeomPoint X=302.996 Y=-79.2541 Z=0
    g121: GeomPoint X=306.073 Y=-77.8102 Z=0
    g122: LineSegment StartX=306.073 StartY=-62.8351 StartZ=0 EndX=306.073 EndY=-77.8102 EndZ=0
    g123: LineSegment StartX=302.996 StartY=-79.2541 StartZ=0 EndX=236.821 EndY=-24.2775 EndZ=0
    g124: LineSegment StartX=238.538 StartY=-21.7539 StartZ=0 EndX=302.567 EndY=-56.9099 EndZ=0
    g125: Circle CenterX=61.6457 CenterY=-88.8112 CenterZ=0 NormalX=0 NormalY=0 NormalZ=1 AngleXU=0 Radius=1
    g126: Circle CenterX=58.0728 CenterY=-91.7794 CenterZ=0 NormalX=0 NormalY=0 NormalZ=1 AngleXU=0 Radius=1
    g127: Circle CenterX=63.9135 CenterY=-91.7791 CenterZ=0 NormalX=0 NormalY=0 NormalZ=1 AngleXU=0 Radius=1
    g128: BSplineCurve PolesCount=3 KnotsCount=2 Degree=2 IsPeriodic=0
    g129: GeomPoint X=61.6457 Y=-88.8112 Z=0
    g130: GeomPoint X=63.9135 Y=-91.7791 Z=0
    g131: Circle CenterX=179.022 CenterY=-85.8163 CenterZ=0 NormalX=0 NormalY=0 NormalZ=1 AngleXU=0 Radius=1
    g132: Circle CenterX=179.022 CenterY=-91.7794 CenterZ=0 NormalX=0 NormalY=0 NormalZ=1 AngleXU=0 Radius=1
    g133: Circle CenterX=171.895 CenterY=-91.7791 CenterZ=0 NormalX=0 NormalY=0 NormalZ=1 AngleXU=0 Radius=1
    g134: BSplineCurve PolesCount=3 KnotsCount=2 Degree=2 IsPeriodic=0
    g135: GeomPoint X=179.022 Y=-85.8163 Z=0
    g136: GeomPoint X=171.895 Y=-91.7791 Z=0
    g137: Circle CenterX=185.124 CenterY=-86.2028 CenterZ=0 NormalX=0 NormalY=0 NormalZ=1 AngleXU=0 Radius=1
    g138: Circle CenterX=185.124 CenterY=-91.7794 CenterZ=0 NormalX=0 NormalY=0 NormalZ=1 AngleXU=0 Radius=1
    g139: Circle CenterX=191.747 CenterY=-91.7794 CenterZ=0 NormalX=0 NormalY=0 NormalZ=1 AngleXU=0 Radius=1
    g140: BSplineCurve PolesCount=3 KnotsCount=2 Degree=2 IsPeriodic=0
    g141: GeomPoint X=185.124 Y=-86.2028 Z=0
    g142: GeomPoint X=191.747 Y=-91.7794 Z=0
    g143: Circle CenterX=299.888 CenterY=-86.6413 CenterZ=0 NormalX=0 NormalY=0 NormalZ=1 AngleXU=0 Radius=1
    g144: Circle CenterX=306.073 CenterY=-91.7794 CenterZ=0 NormalX=0 NormalY=0 NormalZ=1 AngleXU=0 Radius=1
    g145: Circle CenterX=298.776 CenterY=-91.7794 CenterZ=0 NormalX=0 NormalY=0 NormalZ=1 AngleXU=0 Radius=1
    g146: BSplineCurve PolesCount=3 KnotsCount=2 Degree=2 IsPeriodic=0
    g147: GeomPoint X=299.888 Y=-86.6413 Z=0
    g148: GeomPoint X=298.776 Y=-91.7794 Z=0
    g149: LineSegment StartX=189.124 StartY=5.37834 StartZ=0 EndX=299.888 EndY=-86.6413 EndZ=0
    g150: LineSegment StartX=298.776 StartY=-91.7794 StartZ=0 EndX=191.747 EndY=-91.7794 EndZ=0
    g151: LineSegment StartX=185.124 StartY=-86.2028 StartZ=0 EndX=185.124 EndY=5.34704 EndZ=0
    g152: LineSegment StartX=179.022 StartY=5.34704 StartZ=0 EndX=179.022 EndY=-85.8163 EndZ=0
    g153: LineSegment StartX=171.895 StartY=-91.7791 StartZ=0 EndX=63.9135 EndY=-91.7791 EndZ=0
    g154: LineSegment StartX=61.6457 StartY=-88.8112 StartZ=0 EndX=175.022 EndY=5.37834 EndZ=0
    g155: Circle CenterX=302.073 CenterY=124.221 CenterZ=0 NormalX=0 NormalY=0 NormalZ=1 AngleXU=0 Radius=1
    g156: Circle CenterX=306.073 CenterY=124.221 CenterZ=0 NormalX=0 NormalY=0 NormalZ=1 AngleXU=0 Radius=1
    g157: Circle CenterX=302.996 CenterY=121.665 CenterZ=0 NormalX=0 NormalY=0 NormalZ=1 AngleXU=0 Radius=1
    g158: BSplineCurve PolesCount=3 KnotsCount=2 Degree=2 IsPeriodic=0
    g159: GeomPoint X=302.073 Y=124.221 Z=0
    g160: GeomPoint X=302.996 Y=121.665 Z=0
    g161: Circle CenterX=189.124 CenterY=124.221 CenterZ=0 NormalX=0 NormalY=0 NormalZ=1 AngleXU=0 Radius=1
    g162: Circle CenterX=185.124 CenterY=124.221 CenterZ=0 NormalX=0 NormalY=0 NormalZ=1 AngleXU=0 Radius=1
    g163: Circle CenterX=185.124 CenterY=120.221 CenterZ=0 NormalX=0 NormalY=0 NormalZ=1 AngleXU=0 Radius=1
    g164: BSplineCurve PolesCount=3 KnotsCount=2 Degree=2 IsPeriodic=0
    g165: GeomPoint X=189.124 Y=124.221 Z=0
    g166: GeomPoint X=185.124 Y=120.221 Z=0
    g167: Circle CenterX=175.022 CenterY=124.221 CenterZ=0 NormalX=0 NormalY=0 NormalZ=1 AngleXU=0 Radius=1
    g168: Circle CenterX=179.022 CenterY=124.221 CenterZ=0 NormalX=0 NormalY=0 NormalZ=1 AngleXU=0 Radius=1
    g169: Circle CenterX=179.022 CenterY=120.221 CenterZ=0 NormalX=0 NormalY=0 NormalZ=1 AngleXU=0 Radius=1
    g170: BSplineCurve PolesCount=3 KnotsCount=2 Degree=2 IsPeriodic=0
    g171: GeomPoint X=175.022 Y=124.221 Z=0
    g172: GeomPoint X=179.022 Y=120.221 Z=0
    g173: Circle CenterX=62.0728 CenterY=124.221 CenterZ=0 NormalX=0 NormalY=0 NormalZ=1 AngleXU=0 Radius=1
    g174: Circle CenterX=58.0728 CenterY=124.221 CenterZ=0 NormalX=0 NormalY=0 NormalZ=1 AngleXU=0 Radius=1
    g175: Circle CenterX=61.1496 CenterY=121.665 CenterZ=0 NormalX=0 NormalY=0 NormalZ=1 AngleXU=0 Radius=1
    g176: BSplineCurve PolesCount=3 KnotsCount=2 Degree=2 IsPeriodic=0
    g177: GeomPoint X=62.0728 Y=124.221 Z=0
    g178: GeomPoint X=61.1496 Y=121.665 Z=0
    g179: LineSegment StartX=179.022 StartY=120.221 StartZ=0 EndX=179.022 EndY=27.0628 EndZ=0
    g180: LineSegment StartX=185.124 StartY=27.0628 StartZ=0 EndX=185.124 EndY=120.221 EndZ=0
    g181: LineSegment StartX=302.996 StartY=121.665 StartZ=0 EndX=189.124 EndY=27.0628 EndZ=0
    g182: LineSegment StartX=175.022 StartY=27.0628 StartZ=0 EndX=61.1496 EndY=121.665 EndZ=0
    g183: Circle CenterX=61.5791 CenterY=75.4095 CenterZ=0 NormalX=0 NormalY=0 NormalZ=1 AngleXU=0 Radius=1
    g184: Circle CenterX=58.0728 CenterY=77.3346 CenterZ=0 NormalX=0 NormalY=0 NormalZ=1 AngleXU=0 Radius=1
    g185: Circle CenterX=58.0728 CenterY=73.3346 CenterZ=0 NormalX=0 NormalY=0 NormalZ=1 AngleXU=0 Radius=1
    g186: BSplineCurve PolesCount=3 KnotsCount=2 Degree=2 IsPeriodic=0
    g187: GeomPoint X=61.5791 Y=75.4095 Z=0
    g188: GeomPoint X=58.0728 Y=73.3346 Z=0
    g189: Circle CenterX=58.0728 CenterY=-40.8935 CenterZ=0 NormalX=0 NormalY=0 NormalZ=1 AngleXU=0 Radius=1
    g190: Circle CenterX=58.0728 CenterY=-44.8935 CenterZ=0 NormalX=0 NormalY=0 NormalZ=1 AngleXU=0 Radius=1
    g191: Circle CenterX=61.5791 CenterY=-42.9683 CenterZ=0 NormalX=0 NormalY=0 NormalZ=1 AngleXU=0 Radius=1
    g192: BSplineCurve PolesCount=3 KnotsCount=2 Degree=2 IsPeriodic=0
    g193: GeomPoint X=58.0728 Y=-40.8935 Z=0
    g194: GeomPoint X=61.5791 Y=-42.9683 Z=0
    g195: LineSegment StartX=61.5791 StartY=-42.9683 StartZ=0 EndX=165.871 EndY=14.2954 EndZ=0
    g196: LineSegment StartX=165.871 StartY=18.1458 StartZ=0 EndX=61.5791 EndY=75.4095 EndZ=0
    g197: LineSegment StartX=58.0728 StartY=73.3346 StartZ=0 EndX=58.0728 EndY=-40.8935 EndZ=0
    g198: Circle CenterX=302.567 CenterY=-42.9683 CenterZ=0 NormalX=0 NormalY=0 NormalZ=1 AngleXU=0 Radius=1
    g199: Circle CenterX=306.073 CenterY=-44.8935 CenterZ=0 NormalX=0 NormalY=0 NormalZ=1 AngleXU=0 Radius=1
    g200: Circle CenterX=306.073 CenterY=-40.8935 CenterZ=0 NormalX=0 NormalY=0 NormalZ=1 AngleXU=0 Radius=1
    g201: BSplineCurve PolesCount=3 KnotsCount=2 Degree=2 IsPeriodic=0
    g202: GeomPoint X=302.567 Y=-42.9683 Z=0
    g203: GeomPoint X=306.073 Y=-40.8935 Z=0
    g204: Circle CenterX=306.073 CenterY=73.3346 CenterZ=0 NormalX=0 NormalY=0 NormalZ=1 AngleXU=0 Radius=1
    g205: Circle CenterX=306.073 CenterY=77.3346 CenterZ=0 NormalX=0 NormalY=0 NormalZ=1 AngleXU=0 Radius=1
    g206: Circle CenterX=302.567 CenterY=75.4095 CenterZ=0 NormalX=0 NormalY=0 NormalZ=1 AngleXU=0 Radius=1
    g207: BSplineCurve PolesCount=3 KnotsCount=2 Degree=2 IsPeriodic=0
    g208: GeomPoint X=306.073 Y=73.3346 Z=0
    g209: GeomPoint X=302.567 Y=75.4095 Z=0
    g210: LineSegment StartX=302.567 StartY=-42.9683 StartZ=0 EndX=198.275 EndY=14.2954 EndZ=0
    g211: LineSegment StartX=198.275 StartY=18.1458 StartZ=0 EndX=302.567 EndY=75.4095 EndZ=0
    g212: LineSegment StartX=306.073 StartY=73.3346 StartZ=0 EndX=306.073 EndY=-40.8935 EndZ=0
    g213: LineSegment StartX=322.073 StartY=105.865 StartZ=0 EndX=328.643 EndY=105.865 EndZ=0
    g214: LineSegment StartX=318.073 StartY=120.221 StartZ=0 EndX=318.073 EndY=109.865 EndZ=0
    g215: LineSegment StartX=336.157 StartY=107.779 StartZ=0 EndX=362.567 EndY=122.294 EndZ=0
    g216: Circle CenterX=362.073 CenterY=124.221 CenterZ=0 NormalX=0 NormalY=0 NormalZ=1 AngleXU=0 Radius=1
    g217: Circle CenterX=366.073 CenterY=124.221 CenterZ=0 NormalX=0 NormalY=0 NormalZ=1 AngleXU=0 Radius=1
    g218: Circle CenterX=362.567 CenterY=122.294 CenterZ=0 NormalX=0 NormalY=0 NormalZ=1 AngleXU=0 Radius=1
    g219: BSplineCurve PolesCount=3 KnotsCount=2 Degree=2 IsPeriodic=0
    g220: GeomPoint X=362.073 Y=124.221 Z=0
    g221: GeomPoint X=362.567 Y=122.294 Z=0
    g222: Circle CenterX=322.073 CenterY=124.221 CenterZ=0 NormalX=0 NormalY=0 NormalZ=1 AngleXU=0 Radius=1
    g223: Circle CenterX=318.073 CenterY=124.221 CenterZ=0 NormalX=0 NormalY=0 NormalZ=1 AngleXU=0 Radius=1
    g224: Circle CenterX=318.073 CenterY=120.221 CenterZ=0 NormalX=0 NormalY=0 NormalZ=1 AngleXU=0 Radius=1
    g225: BSplineCurve PolesCount=3 KnotsCount=2 Degree=2 IsPeriodic=0
    g226: GeomPoint X=322.073 Y=124.221 Z=0
    g227: GeomPoint X=318.073 Y=120.221 Z=0
    g228: Circle CenterX=322.073 CenterY=105.865 CenterZ=0 NormalX=0 NormalY=0 NormalZ=1 AngleXU=0 Radius=1
    g229: Circle CenterX=318.073 CenterY=105.865 CenterZ=0 NormalX=0 NormalY=0 NormalZ=1 AngleXU=0 Radius=1
    g230: Circle CenterX=318.073 CenterY=109.865 CenterZ=0 NormalX=0 NormalY=0 NormalZ=1 AngleXU=0 Radius=1
    g231: BSplineCurve PolesCount=3 KnotsCount=2 Degree=2 IsPeriodic=0
    g232: GeomPoint X=322.073 Y=105.865 Z=0
    g233: GeomPoint X=318.073 Y=109.865 Z=0
    g234: Circle CenterX=336.157 CenterY=107.779 CenterZ=0 NormalX=0 NormalY=0 NormalZ=1 AngleXU=0 Radius=1
    g235: Circle CenterX=332.651 CenterY=105.853 CenterZ=0 NormalX=0 NormalY=0 NormalZ=1 AngleXU=0 Radius=1
    g236: Circle CenterX=328.643 CenterY=105.865 CenterZ=0 NormalX=0 NormalY=0 NormalZ=1 AngleXU=0 Radius=1
    g237: BSplineCurve PolesCount=3 KnotsCount=2 Degree=2 IsPeriodic=0
    g238: GeomPoint X=336.157 Y=107.779 Z=0
    g239: GeomPoint X=328.643 Y=105.865 Z=0
    g240: LineSegment StartX=322.073 StartY=124.221 StartZ=0 EndX=362.073 EndY=124.221 EndZ=0
    g241: Circle CenterX=371.567 CenterY=-80.8644 CenterZ=0 NormalX=0 NormalY=0 NormalZ=1 AngleXU=0 Radius=1
    g242: Circle CenterX=375.073 CenterY=-82.7896 CenterZ=0 NormalX=0 NormalY=0 NormalZ=1 AngleXU=0 Radius=1
    g243: Circle CenterX=375.073 CenterY=-78.7896 CenterZ=0 NormalX=0 NormalY=0 NormalZ=1 AngleXU=0 Radius=1
    g244: BSplineCurve PolesCount=3 KnotsCount=2 Degree=2 IsPeriodic=0
    g245: GeomPoint X=371.567 Y=-80.8644 Z=0
    g246: GeomPoint X=375.073 Y=-78.7896 Z=0
    g247: Circle CenterX=321.579 CenterY=-53.4075 CenterZ=0 NormalX=0 NormalY=0 NormalZ=1 AngleXU=0 Radius=1
    g248: Circle CenterX=318.073 CenterY=-51.4823 CenterZ=0 NormalX=0 NormalY=0 NormalZ=1 AngleXU=0 Radius=1
    g249: Circle CenterX=318.073 CenterY=-47.4805 CenterZ=0 NormalX=0 NormalY=0 NormalZ=1 AngleXU=0 Radius=1
    g250: BSplineCurve PolesCount=3 KnotsCount=2 Degree=2 IsPeriodic=0
    g251: GeomPoint X=321.579 Y=-53.4075 Z=0
    g252: GeomPoint X=318.073 Y=-47.4805 Z=0
    g253: LineSegment StartX=371.567 StartY=-80.8644 StartZ=0 EndX=321.579 EndY=-53.4075 EndZ=0
    g254: Circle CenterX=321.579 CenterY=-67.3492 CenterZ=0 NormalX=0 NormalY=0 NormalZ=1 AngleXU=0 Radius=1
    g255: Circle CenterX=318.073 CenterY=-65.424 CenterZ=0 NormalX=0 NormalY=0 NormalZ=1 AngleXU=0 Radius=1
    g256: Circle CenterX=318.073 CenterY=-69.424 CenterZ=0 NormalX=0 NormalY=0 NormalZ=1 AngleXU=0 Radius=1
    g257: BSplineCurve PolesCount=3 KnotsCount=2 Degree=2 IsPeriodic=0
    g258: GeomPoint X=321.579 Y=-67.3492 Z=0
    g259: GeomPoint X=318.073 Y=-69.424 Z=0
    g260: Circle CenterX=362.567 CenterY=-89.8542 CenterZ=0 NormalX=0 NormalY=0 NormalZ=1 AngleXU=0 Radius=1
    g261: Circle CenterX=366.073 CenterY=-91.7794 CenterZ=0 NormalX=0 NormalY=0 NormalZ=1 AngleXU=0 Radius=1
    g262: Circle CenterX=362.073 CenterY=-91.7794 CenterZ=0 NormalX=0 NormalY=0 NormalZ=1 AngleXU=0 Radius=1
    g263: BSplineCurve PolesCount=3 KnotsCount=2 Degree=2 IsPeriodic=0
    g264: GeomPoint X=362.567 Y=-89.8542 Z=0
    g265: GeomPoint X=362.073 Y=-91.7794 Z=0
    g266: Circle CenterX=322.073 CenterY=-91.7794 CenterZ=0 NormalX=0 NormalY=0 NormalZ=1 AngleXU=0 Radius=1
    g267: Circle CenterX=318.073 CenterY=-91.7794 CenterZ=0 NormalX=0 NormalY=0 NormalZ=1 AngleXU=0 Radius=1
    g268: Circle CenterX=318.073 CenterY=-87.7794 CenterZ=0 NormalX=0 NormalY=0 NormalZ=1 AngleXU=0 Radius=1
    g269: BSplineCurve PolesCount=3 KnotsCount=2 Degree=2 IsPeriodic=0
    g270: GeomPoint X=322.073 Y=-91.7794 Z=0
    g271: GeomPoint X=318.073 Y=-87.7794 Z=0
    g272: LineSegment StartX=362.567 StartY=-89.8542 StartZ=0 EndX=321.579 EndY=-67.3492 EndZ=0
    g273: LineSegment StartX=318.073 StartY=-69.424 StartZ=0 EndX=318.073 EndY=-87.7794 EndZ=0
    g274: LineSegment StartX=322.073 StartY=-91.7794 StartZ=0 EndX=362.073 EndY=-91.7794 EndZ=0
    g275: Circle CenterX=2.07281 CenterY=124.221 CenterZ=0 NormalX=0 NormalY=0 NormalZ=1 AngleXU=0 Radius=1
    g276: Circle CenterX=1.57905 CenterY=122.295 CenterZ=0 NormalX=0 NormalY=0 NormalZ=1 AngleXU=0 Radius=1
    g277: BSplineCurve PolesCount=3 KnotsCount=2 Degree=2 IsPeriodic=0
    g278: GeomPoint X=2.07281 Y=124.221 Z=0
    g279: GeomPoint X=1.57905 Y=122.295 Z=0
    g280: Circle CenterX=42.0728 CenterY=124.221 CenterZ=0 NormalX=0 NormalY=0 NormalZ=1 AngleXU=0 Radius=1
    g281: Circle CenterX=46.0728 CenterY=124.221 CenterZ=0 NormalX=0 NormalY=0 NormalZ=1 AngleXU=0 Radius=1
    g282: Circle CenterX=46.0728 CenterY=120.221 CenterZ=0 NormalX=0 NormalY=0 NormalZ=1 AngleXU=0 Radius=1
    g283: BSplineCurve PolesCount=3 KnotsCount=2 Degree=2 IsPeriodic=0
    g284: GeomPoint X=42.0728 Y=124.221 Z=0
    g285: GeomPoint X=46.0728 Y=120.221 Z=0
    g286: Circle CenterX=46.0728 CenterY=109.865 CenterZ=0 NormalX=0 NormalY=0 NormalZ=1 AngleXU=0 Radius=1
    g287: Circle CenterX=46.0728 CenterY=105.865 CenterZ=0 NormalX=0 NormalY=0 NormalZ=1 AngleXU=0 Radius=1
    g288: Circle CenterX=42.0728 CenterY=105.865 CenterZ=0 NormalX=0 NormalY=0 NormalZ=1 AngleXU=0 Radius=1
    g289: BSplineCurve PolesCount=3 KnotsCount=2 Degree=2 IsPeriodic=0
    g290: GeomPoint X=46.0728 Y=109.865 Z=0
    g291: GeomPoint X=42.0728 Y=105.865 Z=0
    g292: Circle CenterX=35.5028 CenterY=105.865 CenterZ=0 NormalX=0 NormalY=0 NormalZ=1 AngleXU=0 Radius=1
    g293: Circle CenterX=31.5028 CenterY=105.865 CenterZ=0 NormalX=0 NormalY=0 NormalZ=1 AngleXU=0 Radius=1
    g294: Circle CenterX=27.9965 CenterY=107.79 CenterZ=0 NormalX=0 NormalY=0 NormalZ=1 AngleXU=0 Radius=1
    g295: BSplineCurve PolesCount=3 KnotsCount=2 Degree=2 IsPeriodic=0
    g296: GeomPoint X=35.5028 Y=105.865 Z=0
    g297: GeomPoint X=27.9965 Y=107.79 Z=0
    g298: LineSegment StartX=2.07281 StartY=124.221 StartZ=0 EndX=42.0728 EndY=124.221 EndZ=0
    g299: LineSegment StartX=46.0728 StartY=120.221 StartZ=0 EndX=46.0728 EndY=109.865 EndZ=0
    g300: LineSegment StartX=42.0728 StartY=105.865 StartZ=0 EndX=35.5028 EndY=105.865 EndZ=0
    g301: LineSegment StartX=27.9965 StartY=107.79 StartZ=0 EndX=1.57905 EndY=122.295 EndZ=0
    g302: Circle CenterX=42.5666 CenterY=-67.3492 CenterZ=0 NormalX=0 NormalY=0 NormalZ=1 AngleXU=0 Radius=1
    g303: Circle CenterX=46.0728 CenterY=-65.424 CenterZ=0 NormalX=0 NormalY=0 NormalZ=1 AngleXU=0 Radius=1
    g304: Circle CenterX=46.0728 CenterY=-69.424 CenterZ=0 NormalX=0 NormalY=0 NormalZ=1 AngleXU=0 Radius=1
    g305: BSplineCurve PolesCount=3 KnotsCount=2 Degree=2 IsPeriodic=0
    g306: GeomPoint X=42.5666 Y=-67.3492 Z=0
    g307: GeomPoint X=46.0728 Y=-69.424 Z=0
    g308: Circle CenterX=46.0728 CenterY=-87.7794 CenterZ=0 NormalX=0 NormalY=0 NormalZ=1 AngleXU=0 Radius=1
    g309: Circle CenterX=46.0728 CenterY=-91.7794 CenterZ=0 NormalX=0 NormalY=0 NormalZ=1 AngleXU=0 Radius=1
    g310: Circle CenterX=42.0728 CenterY=-91.7794 CenterZ=0 NormalX=0 NormalY=0 NormalZ=1 AngleXU=0 Radius=1
    g311: BSplineCurve PolesCount=3 KnotsCount=2 Degree=2 IsPeriodic=0
    g312: GeomPoint X=46.0728 Y=-87.7794 Z=0
    g313: GeomPoint X=42.0728 Y=-91.7794 Z=0
    g314: Circle CenterX=2.07281 CenterY=-91.7794 CenterZ=0 NormalX=0 NormalY=0 NormalZ=1 AngleXU=0 Radius=1
    g315: Circle CenterX=-1.92719 CenterY=-91.7794 CenterZ=0 NormalX=0 NormalY=0 NormalZ=1 AngleXU=0 Radius=1
    g316: Circle CenterX=1.57905 CenterY=-89.8542 CenterZ=0 NormalX=0 NormalY=0 NormalZ=1 AngleXU=0 Radius=1
    g317: BSplineCurve PolesCount=3 KnotsCount=2 Degree=2 IsPeriodic=0
    g318: GeomPoint X=2.07281 Y=-91.7794 Z=0
    g319: GeomPoint X=1.57905 Y=-89.8542 Z=0
    g320: LineSegment StartX=2.07281 StartY=-91.7794 StartZ=0 EndX=42.0728 EndY=-91.7794 EndZ=0
    g321: LineSegment StartX=46.0728 StartY=-87.7794 StartZ=0 EndX=46.0728 EndY=-69.424 EndZ=0
    g322: LineSegment StartX=42.5666 StartY=-67.3492 StartZ=0 EndX=1.57905 EndY=-89.8542 EndZ=0
    g323: Circle CenterX=322.073 CenterY=76.4095 CenterZ=0 NormalX=0 NormalY=0 NormalZ=1 AngleXU=0 Radius=4
    g324: BSplineCurve PolesCount=3 KnotsCount=2 Degree=2 IsPeriodic=0
    g325: GeomPoint X=318.073 Y=72.4095 Z=0
    g326: GeomPoint X=322.073 Y=76.4095 Z=0
    g327: Circle CenterX=375.073 CenterY=72.4095 CenterZ=0 NormalX=0 NormalY=0 NormalZ=1 AngleXU=0 Radius=1
    g328: Circle CenterX=375.073 CenterY=76.4095 CenterZ=0 NormalX=0 NormalY=0 NormalZ=1 AngleXU=0 Radius=1
    g329: Circle CenterX=371.073 CenterY=76.4095 CenterZ=0 NormalX=0 NormalY=0 NormalZ=1 AngleXU=0 Radius=1
    g330: BSplineCurve PolesCount=3 KnotsCount=2 Degree=2 IsPeriodic=0
    g331: GeomPoint X=375.073 Y=72.4095 Z=0
    g332: GeomPoint X=371.073 Y=76.4095 Z=0
    g333: LineSegment StartX=322.073 StartY=76.4095 StartZ=0 EndX=371.073 EndY=76.4095 EndZ=0
    g334: LineSegment StartX=318.073 StartY=72.4095 StartZ=0 EndX=318.073 EndY=-47.4805 EndZ=0
    g335: LineSegment StartX=375.073 StartY=72.4095 StartZ=0 EndX=375.073 EndY=-78.7896 EndZ=0
    g336: ArcOfCircle CenterX=-26.9272 CenterY=22.1087 CenterZ=0 NormalX=0 NormalY=0 NormalZ=1 AngleXU=0 Radius=4 StartAngle=5e-16 EndAngle=3.14159
    g337: LineSegment StartX=-22.9272 StartY=22.1087 StartZ=0 EndX=-18.9272 EndY=-83.7794 EndZ=0
    g338: LineSegment StartX=-34.9272 StartY=-83.7794 StartZ=0 EndX=-30.9272 EndY=22.1087 EndZ=0
    g339: ArcOfCircle CenterX=391.073 CenterY=22.1087 CenterZ=0 NormalX=0 NormalY=0 NormalZ=1 AngleXU=0 Radius=4 StartAngle=0 EndAngle=3.14159
    g340: LineSegment StartX=387.073 StartY=22.1087 StartZ=0 EndX=383.073 EndY=-83.7794 EndZ=0
    g341: LineSegment StartX=395.073 StartY=22.1087 StartZ=0 EndX=399.073 EndY=-83.7794 EndZ=0
    g342: Circle CenterX=-10.9272 CenterY=-78.7794 CenterZ=0 NormalX=0 NormalY=0 NormalZ=1 AngleXU=0 Radius=1
    g343: Circle CenterX=-10.9272 CenterY=-82.7794 CenterZ=0 NormalX=0 NormalY=0 NormalZ=1 AngleXU=0 Radius=1
    g344: Circle CenterX=-7.42095 CenterY=-80.8542 CenterZ=0 NormalX=0 NormalY=0 NormalZ=1 AngleXU=0 Radius=1
    g345: BSplineCurve PolesCount=3 KnotsCount=2 Degree=2 IsPeriodic=0
    g346: GeomPoint X=-10.9272 Y=-78.7794 Z=0
    g347: GeomPoint X=-7.42095 Y=-80.8542 Z=0
    g348: Circle CenterX=42.5666 CenterY=-53.4075 CenterZ=0 NormalX=0 NormalY=0 NormalZ=1 AngleXU=0 Radius=1
    g349: Circle CenterX=46.0728 CenterY=-51.4823 CenterZ=0 NormalX=0 NormalY=0 NormalZ=1 AngleXU=0 Radius=1
    g350: Circle CenterX=46.0728 CenterY=-47.4823 CenterZ=0 NormalX=0 NormalY=0 NormalZ=1 AngleXU=0 Radius=1
    g351: BSplineCurve PolesCount=3 KnotsCount=2 Degree=2 IsPeriodic=0
    g352: GeomPoint X=42.5666 Y=-53.4075 Z=0
    g353: GeomPoint X=46.0728 Y=-47.4823 Z=0
    g354: Circle CenterX=46.0728 CenterY=72.4095 CenterZ=0 NormalX=0 NormalY=0 NormalZ=1 AngleXU=0 Radius=1
    g355: Circle CenterX=46.0728 CenterY=76.4095 CenterZ=0 NormalX=0 NormalY=0 NormalZ=1 AngleXU=0 Radius=1
    g356: Circle CenterX=42.0728 CenterY=76.4095 CenterZ=0 NormalX=0 NormalY=0 NormalZ=1 AngleXU=0 Radius=1
    g357: BSplineCurve PolesCount=3 KnotsCount=2 Degree=2 IsPeriodic=0
    g358: GeomPoint X=46.0728 Y=72.4095 Z=0
    g359: GeomPoint X=42.0728 Y=76.4095 Z=0
    g360: Circle CenterX=-6.92718 CenterY=76.4095 CenterZ=0 NormalX=0 NormalY=0 NormalZ=1 AngleXU=0 Radius=1
    g361: Circle CenterX=-10.9272 CenterY=76.4095 CenterZ=0 NormalX=0 NormalY=0 NormalZ=1 AngleXU=0 Radius=1
    g362: Circle CenterX=-10.9272 CenterY=72.4095 CenterZ=0 NormalX=0 NormalY=0 NormalZ=1 AngleXU=0 Radius=1
    g363: BSplineCurve PolesCount=3 KnotsCount=2 Degree=2 IsPeriodic=0
    g364: GeomPoint X=-6.92718 Y=76.4095 Z=0
    g365: GeomPoint X=-10.9272 Y=72.4095 Z=0
    g366: LineSegment StartX=-10.9272 StartY=72.4095 StartZ=0 EndX=-10.9272 EndY=-78.7794 EndZ=0
    g367: LineSegment StartX=-7.42095 StartY=-80.8542 StartZ=0 EndX=42.5666 EndY=-53.4075 EndZ=0
    g368: LineSegment StartX=46.0728 StartY=-47.4823 StartZ=0 EndX=46.0728 EndY=72.4095 EndZ=0
    g369: LineSegment StartX=42.0728 StartY=76.4095 StartZ=0 EndX=-6.92719 EndY=76.4095 EndZ=0
    g370: LineSegment StartX=119.072 StartY=136.221 StartZ=0 EndX=119.072 EndY=-116.228 EndZ=0
    g371: LineSegment StartX=-42.9272 StartY=136.221 StartZ=0 EndX=407.073 EndY=136.221 EndZ=0
    g372: LineSegment StartX=232.072 StartY=136.221 StartZ=0 EndX=220.072 EndY=136.221 EndZ=0
    g373: LineSegment StartX=232.072 StartY=136.221 StartZ=0 EndX=232.072 EndY=124.221 EndZ=0
    g374: LineSegment StartX=220.072 StartY=136.221 StartZ=0 EndX=220.072 EndY=124.221 EndZ=0
    g375: LineSegment StartX=220.072 StartY=136.221 StartZ=0 EndX=226.072 EndY=136.221 EndZ=0
    g376: LineSegment StartX=220.072 StartY=136.221 StartZ=0 EndX=220.072 EndY=130.221 EndZ=0
    g377: LineSegment StartX=220.072 StartY=124.221 StartZ=0 EndX=226.072 EndY=124.221 EndZ=0
    g378: LineSegment StartX=232.072 StartY=124.221 StartZ=0 EndX=232.072 EndY=127.221 EndZ=0
    g379: LineSegment StartX=232.072 StartY=136.221 StartZ=0 EndX=232.072 EndY=133.221 EndZ=0
    g380-g384: Circle x5 (B-spline internal-alignment scaffolding for g385; pole/knot coordinates omitted)
    g385: BSplineCurve PolesCount=5 KnotsCount=3 Degree=3 IsPeriodic=0
    g386: GeomPoint X=232.072 Y=133.221 Z=0
    g387: GeomPoint X=223.072 Y=130.221 Z=0
    g388: GeomPoint X=232.072 Y=127.221 Z=0
    g389: LineSegment StartX=189.124 StartY=124.221 StartZ=0 EndX=302.073 EndY=124.221 EndZ=0
    g390: LineSegment StartX=132.072 StartY=136.221 StartZ=0 EndX=132.072 EndY=124.221 EndZ=0
    g391: LineSegment StartX=132.072 StartY=136.221 StartZ=0 EndX=144.072 EndY=136.221 EndZ=0
    g392: LineSegment StartX=144.072 StartY=136.221 StartZ=0 EndX=144.072 EndY=124.221 EndZ=0
    g393: LineSegment StartX=144.072 StartY=136.221 StartZ=0 EndX=138.072 EndY=136.221 EndZ=0
    g394: LineSegment StartX=144.072 StartY=136.221 StartZ=0 EndX=144.072 EndY=130.221 EndZ=0
    g395: LineSegment StartX=132.072 StartY=136.221 StartZ=0 EndX=132.072 EndY=133.221 EndZ=0
    g396: LineSegment StartX=132.072 StartY=133.221 StartZ=0 EndX=132.072 EndY=127.221 EndZ=0
    g397-g401: Circle x5 (B-spline internal-alignment scaffolding for g402; pole/knot coordinates omitted)
    g402: BSplineCurve PolesCount=5 KnotsCount=3 Degree=3 IsPeriodic=0
    g403: GeomPoint X=132.072 Y=133.221 Z=0
    g404: GeomPoint X=141.072 Y=130.221 Z=0
    g405: GeomPoint X=132.072 Y=127.221 Z=0
    g406: LineSegment StartX=132.072 StartY=124.221 StartZ=0 EndX=175.022 EndY=124.221 EndZ=0
    g407: LineSegment StartX=62.0728 StartY=124.221 StartZ=0 EndX=132.072 EndY=124.221 EndZ=0
    ... +17 more geometry lines
  constraints (721):
    c: Vertical(g0)
    c: Vertical(g1)
    c: Block(g1)
    c: Block(g0)
    c: Weight(g4) = 1
    c: Equal(g4,g5)
    c: Equal(g4,g6)
    c: InternalAlignment(g4,g7)
    c: InternalAlignment(g5,g7)
    c: InternalAlignment(g6,g7)
    c: InternalAlignment(g8,g7)
    c: InternalAlignment(g9,g7)
    c: Weight(g10) = 1
    c: Equal(g10,g11)
    c: Equal(g10,g12)
    c: InternalAlignment(g10,g13)
    c: InternalAlignment(g11,g13)
    c: InternalAlignment(g12,g13)
    c: InternalAlignment(g14,g13)
    c: InternalAlignment(g15,g13)
    c: Block(g13)
    c: Block(g7)
    c: Weight(g16) = 1
    c: Equal(g16,g17)
    c: Equal(g16,g18)
    c: InternalAlignment(g16,g19)
    c: InternalAlignment(g17,g19)
    c: InternalAlignment(g18,g19)
    c: InternalAlignment(g20,g19)
    c: InternalAlignment(g21,g19)
    c: Weight(g22) = 1
    c: Equal(g22,g23)
    c: Equal(g22,g24)
    c: InternalAlignment(g22,g25)
    c: InternalAlignment(g23,g25)
    c: InternalAlignment(g24,g25)
    c: InternalAlignment(g26,g25)
    c: InternalAlignment(g27,g25)
    c: Block(g25)
    c: Block(g19)
    c: Weight(g28) = 1
    c: Equal(g28,g29)
    c: Equal(g28,g30)
    c: InternalAlignment(g28,g31)
    c: InternalAlignment(g29,g31)
    c: InternalAlignment(g30,g31)
    c: InternalAlignment(g32,g31)
    c: InternalAlignment(g33,g31)
    c: Weight(g34) = 1
    c: Equal(g34,g35)
    c: Equal(g34,g36)
    c: InternalAlignment(g34,g37)
    c: InternalAlignment(g35,g37)
    c: InternalAlignment(g36,g37)
    c: InternalAlignment(g38,g37)
    c: InternalAlignment(g39,g37)
    c: Block(g31)
    c: Block(g37)
    c: Coincident(g40,g1)
    c: Coincident(g40,g0)
    c: Horizontal(g40)
    c: Distance(g40) = 450
    c: Weight(g41) = 1
    c: Equal(g41,g42)
    c: Equal(g41,g43)
    c: InternalAlignment(g41,g44)
    c: InternalAlignment(g42,g44)
    c: InternalAlignment(g43,g44)
    c: InternalAlignment(g45,g44)
    c: InternalAlignment(g46,g44)
    c: Block(g44)
    c: Weight(g47) = 1
    c: Equal(g47,g48)
    c: Equal(g47,g49)
    c: InternalAlignment(g47,g50)
    c: InternalAlignment(g48,g50)
    c: InternalAlignment(g49,g50)
    c: InternalAlignment(g51,g50)
    c: InternalAlignment(g52,g50)
    c: Block(g50)
    c: Weight(g53) = 1
    c: Equal(g53,g54)
    c: Equal(g53,g55)
    c: InternalAlignment(g53,g56)
    c: InternalAlignment(g54,g56)
    c: InternalAlignment(g55,g56)
    c: InternalAlignment(g57,g56)
    c: InternalAlignment(g58,g56)
    c: Block(g56)
    c: Weight(g59) = 1
    c: Equal(g59,g60)
    c: Equal(g59,g61)
    c: InternalAlignment(g59,g62)
    c: InternalAlignment(g60,g62)
    c: InternalAlignment(g61,g62)
    c: InternalAlignment(g63,g62)
    c: InternalAlignment(g64,g62)
    c: Block(g62)
    c: Weight(g65) = 1
    c: Equal(g65,g66)
    c: Equal(g65,g67)
    c: InternalAlignment(g65,g68)
    c: InternalAlignment(g66,g68)
    c: InternalAlignment(g67,g68)
    c: InternalAlignment(g69,g68)
    c: InternalAlignment(g70,g68)
    c: Weight(g71) = 1
    c: Equal(g71,g72)
    c: Equal(g71,g73)
    c: InternalAlignment(g71,g74)
    c: InternalAlignment(g72,g74)
    c: InternalAlignment(g73,g74)
    c: InternalAlignment(g75,g74)
    c: InternalAlignment(g76,g74)
    c: Block(g68)
    c: Block(g74)
    c: Coincident(g77,g68)
    c: Coincident(g77,g74)
    c: Vertical(g77)
    c: Coincident(g78,g68)
    c: Coincident(g78,g50)
    c: Coincident(g79,g50)
    c: Coincident(g79,g74)
    c: Weight(g80) = 1
    c: Equal(g80,g81)
    c: Equal(g80,g82)
    c: InternalAlignment(g80,g83)
    c: InternalAlignment(g81,g83)
    c: InternalAlignment(g82,g83)
    c: InternalAlignment(g84,g83)
    c: InternalAlignment(g85,g83)
    c: Weight(g86) = 1
    c: Equal(g86,g87)
    c: Equal(g86,g88)
    c: InternalAlignment(g86,g89)
    c: InternalAlignment(g87,g89)
    c: InternalAlignment(g88,g89)
    c: InternalAlignment(g90,g89)
    c: InternalAlignment(g91,g89)
    c: Block(g83)
    c: Block(g89)
    c: Coincident(g92,g83)
    c: Coincident(g92,g89)
    c: Vertical(g92)
    c: Coincident(g93,g83)
    c: Coincident(g93,g44)
    c: Coincident(g94,g44)
    c: Coincident(g94,g89)
    c: Weight(g95) = 1
    c: Equal(g95,g96)
    c: Equal(g95,g97)
    c: InternalAlignment(g95,g98)
    c: InternalAlignment(g96,g98)
    c: InternalAlignment(g97,g98)
    c: InternalAlignment(g99,g98)
    c: InternalAlignment(g100,g98)
    c: Weight(g101) = 1
    c: Equal(g101,g102)
    c: Equal(g101,g103)
    c: InternalAlignment(g101,g104)
    c: InternalAlignment(g102,g104)
    c: InternalAlignment(g103,g104)
    c: InternalAlignment(g105,g104)
    c: InternalAlignment(g106,g104)
    c: Block(g98)
    c: Block(g104)
    c: Coincident(g107,g98)
    c: Coincident(g107,g104)
    c: Vertical(g107)
    c: Coincident(g108,g104)
    c: Coincident(g108,g62)
    c: Coincident(g109,g62)
    c: Coincident(g109,g98)
    c: Weight(g110) = 1
    c: Equal(g110,g111)
    c: Equal(g110,g112)
    c: InternalAlignment(g110,g113)
    c: InternalAlignment(g111,g113)
    c: InternalAlignment(g112,g113)
    c: InternalAlignment(g114,g113)
    c: InternalAlignment(g115,g113)
    c: Weight(g116) = 1
    c: Equal(g116,g117)
    c: Equal(g116,g118)
    c: InternalAlignment(g116,g119)
    c: InternalAlignment(g117,g119)
    c: InternalAlignment(g118,g119)
    c: InternalAlignment(g120,g119)
    c: InternalAlignment(g121,g119)
    c: Block(g113)
    c: Block(g119)
    c: Coincident(g122,g113)
    c: Coincident(g122,g119)
    c: Vertical(g122)
    c: Coincident(g123,g119)
    c: Coincident(g123,g56)
    c: Coincident(g124,g56)
    c: Coincident(g124,g113)
    c: Weight(g125) = 1
    c: Equal(g125,g126)
    c: Equal(g125,g127)
    c: InternalAlignment(g125,g128)
    c: InternalAlignment(g126,g128)
    c: InternalAlignment(g127,g128)
    c: InternalAlignment(g129,g128)
    c: InternalAlignment(g130,g128)
    c: Weight(g131) = 1
    c: Equal(g131,g132)
    c: Equal(g131,g133)
    c: InternalAlignment(g131,g134)
    c: InternalAlignment(g132,g134)
    c: InternalAlignment(g133,g134)
    c: InternalAlignment(g135,g134)
    c: InternalAlignment(g136,g134)
    c: Weight(g137) = 1
    c: Equal(g137,g138)
    c: Equal(g137,g139)
    c: InternalAlignment(g137,g140)
    c: InternalAlignment(g138,g140)
    c: InternalAlignment(g139,g140)
    c: InternalAlignment(g141,g140)
    c: InternalAlignment(g142,g140)
    c: Weight(g143) = 1
    c: Equal(g143,g144)
    c: Equal(g143,g145)
    c: InternalAlignment(g143,g146)
    c: InternalAlignment(g144,g146)
    c: InternalAlignment(g145,g146)
    c: InternalAlignment(g147,g146)
    c: InternalAlignment(g148,g146)
    c: Block(g146)
    c: Block(g140)
    c: Block(g134)
    c: Block(g128)
    c: Coincident(g149,g25)
    c: Coincident(g149,g146)
    c: Coincident(g150,g146)
    c: Coincident(g150,g140)
    c: Horizontal(g150)
    c: Coincident(g151,g140)
    c: Coincident(g151,g25)
    c: Vertical(g151)
    c: Coincident(g152,g19)
    c: Coincident(g152,g134)
    c: Vertical(g152)
    c: Coincident(g153,g134)
    c: Coincident(g153,g128)
    c: Horizontal(g153)
    c: Coincident(g154,g128)
    c: Coincident(g154,g19)
    c: Weight(g155) = 1
    c: Equal(g155,g156)
    c: Equal(g155,g157)
    c: InternalAlignment(g155,g158)
    c: InternalAlignment(g156,g158)
    c: InternalAlignment(g157,g158)
    c: InternalAlignment(g159,g158)
    c: InternalAlignment(g160,g158)
    c: Weight(g161) = 1
    c: Equal(g161,g162)
    c: Equal(g161,g163)
    c: InternalAlignment(g161,g164)
    c: InternalAlignment(g162,g164)
    c: InternalAlignment(g163,g164)
    c: InternalAlignment(g165,g164)
    c: InternalAlignment(g166,g164)
    c: Weight(g167) = 1
    c: Equal(g167,g168)
    c: Equal(g167,g169)
    c: InternalAlignment(g167,g170)
    c: InternalAlignment(g168,g170)
    c: InternalAlignment(g169,g170)
    c: InternalAlignment(g171,g170)
    c: InternalAlignment(g172,g170)
    c: Weight(g173) = 1
    c: Equal(g173,g174)
    c: Equal(g173,g175)
    c: InternalAlignment(g173,g176)
    c: InternalAlignment(g174,g176)
    c: InternalAlignment(g175,g176)
    c: InternalAlignment(g177,g176)
    c: InternalAlignment(g178,g176)
    c: Block(g176)
    c: Block(g170)
    c: Block(g164)
    c: Block(g158)
    c: Coincident(g179,g170)
    c: Coincident(g179,g7)
    c: Vertical(g179)
    c: Coincident(g180,g13)
    c: Coincident(g180,g164)
    c: Vertical(g180)
    c: Coincident(g181,g158)
    c: Coincident(g181,g13)
    c: Coincident(g182,g7)
    c: Weight(g183) = 1
    c: Equal(g183,g184)
    c: Equal(g183,g185)
    c: InternalAlignment(g183,g186)
    c: InternalAlignment(g184,g186)
    c: InternalAlignment(g185,g186)
    c: InternalAlignment(g187,g186)
    c: InternalAlignment(g188,g186)
    c: Weight(g189) = 1
    c: Equal(g189,g190)
    c: Equal(g189,g191)
    c: InternalAlignment(g189,g192)
    c: InternalAlignment(g190,g192)
    c: InternalAlignment(g191,g192)
    c: InternalAlignment(g193,g192)
    c: InternalAlignment(g194,g192)
    c: Block(g192)
    c: Block(g186)
    c: Coincident(g195,g192)
    c: Coincident(g195,g31)
    c: Coincident(g196,g31)
    c: Coincident(g196,g186)
    c: Coincident(g197,g186)
    c: Coincident(g197,g192)
    c: Vertical(g197)
    c: Weight(g198) = 1
    c: Equal(g198,g199)
    c: Equal(g198,g200)
    c: InternalAlignment(g198,g201)
    c: InternalAlignment(g199,g201)
    c: InternalAlignment(g200,g201)
    c: InternalAlignment(g202,g201)
    c: InternalAlignment(g203,g201)
    c: Weight(g204) = 1
    c: Equal(g204,g205)
    c: Equal(g204,g206)
    c: InternalAlignment(g204,g207)
    c: InternalAlignment(g205,g207)
    c: InternalAlignment(g206,g207)
    c: InternalAlignment(g208,g207)
    c: InternalAlignment(g209,g207)
    c: Block(g207)
    c: Block(g201)
    c: Coincident(g210,g201)
    c: Coincident(g210,g37)
    c: Coincident(g211,g37)
    c: Coincident(g211,g207)
    c: Coincident(g212,g207)
    c: Coincident(g212,g201)
    c: Vertical(g212)
    c: Horizontal(g213)
    c: Block(g213)
    c: Vertical(g214)
    c: Block(g214)
    c: Block(g215)
    c: Weight(g216) = 1
    c: Equal(g216,g217)
    c: Equal(g216,g218)
    c: InternalAlignment(g216,g219)
    c: InternalAlignment(g217,g219)
    c: InternalAlignment(g218,g219)
    c: InternalAlignment(g220,g219)
    c: InternalAlignment(g221,g219)
    c: Weight(g222) = 1
    c: Equal(g222,g223)
    c: Equal(g222,g224)
    c: InternalAlignment(g222,g225)
    c: InternalAlignment(g223,g225)
    c: InternalAlignment(g224,g225)
    c: InternalAlignment(g226,g225)
    c: InternalAlignment(g227,g225)
    c: Weight(g228) = 1
    c: Equal(g228,g229)
    c: Equal(g228,g230)
    c: InternalAlignment(g228,g231)
    c: InternalAlignment(g229,g231)
    c: InternalAlignment(g230,g231)
    c: InternalAlignment(g232,g231)
    c: InternalAlignment(g233,g231)
    c: Weight(g234) = 1
    c: Equal(g234,g235)
    c: Equal(g234,g236)
    c: InternalAlignment(g234,g237)
    c: InternalAlignment(g235,g237)
    c: InternalAlignment(g236,g237)
    c: InternalAlignment(g238,g237)
    c: InternalAlignment(g239,g237)
    c: Block(g219)
    c: Block(g225)
    c: Block(g231)
    c: Block(g237)
    c: Coincident(g240,g225)
    c: Coincident(g240,g219)
    c: Horizontal(g240)
    c: Block(g182)
    c: Weight(g241) = 1
    c: Equal(g241,g242)
    c: Equal(g241,g243)
    c: InternalAlignment(g241,g244)
    c: InternalAlignment(g242,g244)
    c: InternalAlignment(g243,g244)
    c: InternalAlignment(g245,g244)
    c: InternalAlignment(g246,g244)
    c: Weight(g247) = 1
    c: Equal(g247,g248)
    c: Equal(g247,g249)
    c: InternalAlignment(g247,g250)
    c: InternalAlignment(g248,g250)
    c: InternalAlignment(g249,g250)
    c: InternalAlignment(g251,g250)
    c: InternalAlignment(g252,g250)
    c: Block(g244)
    c: Block(g250)
    c: Coincident(g253,g244)
    c: Coincident(g253,g250)
    c: Weight(g254) = 1
    c: Equal(g254,g255)
    c: Equal(g254,g256)
    c: InternalAlignment(g254,g257)
    c: InternalAlignment(g255,g257)
    c: InternalAlignment(g256,g257)
    c: InternalAlignment(g258,g257)
    c: InternalAlignment(g259,g257)
    c: Weight(g260) = 1
    c: Equal(g260,g261)
    c: Equal(g260,g262)
    c: InternalAlignment(g260,g263)
    c: InternalAlignment(g261,g263)
    c: InternalAlignment(g262,g263)
    c: InternalAlignment(g264,g263)
    c: InternalAlignment(g265,g263)
    c: Weight(g266) = 1
    c: Equal(g266,g267)
    c: Equal(g266,g268)
    c: InternalAlignment(g266,g269)
    c: InternalAlignment(g267,g269)
    c: InternalAlignment(g268,g269)
    c: InternalAlignment(g270,g269)
    c: InternalAlignment(g271,g269)
    c: Block(g269)
    c: Block(g263)
    c: Block(g257)
    c: Coincident(g272,g263)
    c: Coincident(g272,g257)
    c: Coincident(g273,g257)
    c: Coincident(g273,g269)
    c: Vertical(g273)
    c: Coincident(g274,g269)
    c: Coincident(g274,g263)
    c: Horizontal(g274)
    c: Weight(g275) = 1
    c: Equal(g275,g276)
    c: InternalAlignment(g275,g277)
    c: InternalAlignment(g276,g277)
    c: InternalAlignment(g278,g277)
    c: InternalAlignment(g279,g277)
    c: Weight(g280) = 1
    c: InternalAlignment(g281,g283)
    c: InternalAlignment(g282,g283)
    c: InternalAlignment(g284,g283)
    c: InternalAlignment(g285,g283)
    c: Weight(g286) = 1
    c: Equal(g286,g287)
    c: Equal(g286,g288)
    c: InternalAlignment(g286,g289)
    c: InternalAlignment(g287,g289)
    c: InternalAlignment(g288,g289)
    c: InternalAlignment(g290,g289)
    c: InternalAlignment(g291,g289)
    c: Equal(g292,g293)
    c: Equal(g292,g294)
    c: InternalAlignment(g292,g295)
    c: InternalAlignment(g293,g295)
    c: InternalAlignment(g294,g295)
    c: InternalAlignment(g296,g295)
    c: InternalAlignment(g297,g295)
    c: Block(g283)
    c: Block(g289)
    c: Block(g295)
    c: Block(g277)
    c: Coincident(g298,g277)
    c: Coincident(g298,g283)
    c: Horizontal(g298)
    c: Coincident(g299,g283)
    c: Coincident(g299,g289)
    c: Vertical(g299)
    c: Coincident(g300,g289)
    c: Coincident(g300,g295)
    c: Horizontal(g300)
    c: Coincident(g301,g295)
    c: Coincident(g301,g277)
    c: Weight(g302) = 1
    c: Equal(g302,g303)
    c: Equal(g302,g304)
    c: InternalAlignment(g302,g305)
    c: InternalAlignment(g303,g305)
    c: InternalAlignment(g304,g305)
    c: InternalAlignment(g306,g305)
    c: InternalAlignment(g307,g305)
    c: Weight(g308) = 1
    c: Equal(g308,g309)
    c: Equal(g308,g310)
    c: InternalAlignment(g308,g311)
    c: InternalAlignment(g309,g311)
    c: InternalAlignment(g310,g311)
    c: InternalAlignment(g312,g311)
    c: Weight(g314) = 1
    c: Equal(g314,g315)
    c: Equal(g314,g316)
    c: InternalAlignment(g314,g317)
    c: InternalAlignment(g315,g317)
    c: InternalAlignment(g316,g317)
    c: InternalAlignment(g318,g317)
    c: InternalAlignment(g319,g317)
    c: Block(g317)
    c: Block(g311)
    c: Block(g305)
    c: Coincident(g320,g317)
    c: Coincident(g320,g311)
    c: Horizontal(g320)
    c: Coincident(g321,g311)
    c: Coincident(g321,g305)
    c: Vertical(g321)
    c: Coincident(g322,g305)
    c: Coincident(g322,g317)
    c: InternalAlignment(g323,g324)
    c: InternalAlignment(g325,g324)
    c: InternalAlignment(g326,g324)
    c: Block(g324)
    c: Equal(g327,g328)
    c: Equal(g327,g329)
    c: InternalAlignment(g327,g330)
    c: InternalAlignment(g328,g330)
    c: InternalAlignment(g329,g330)
    c: InternalAlignment(g331,g330)
    c: InternalAlignment(g332,g330)
    c: Block(g330)
    c: Coincident(g333,g324)
    c: Horizontal(g333)
    c: Block(g333)
    c: Coincident(g334,g324)
    c: Coincident(g334,g250)
    c: Vertical(g334)
    c: Coincident(g335,g330)
    c: Coincident(g335,g244)
    c: Vertical(g335)
    c: Block(g336)
    c: Block(g2)
    c: Distance(g334) = 119.89
    c: Coincident(g337,g336)
    c: Coincident(g337,g2)
    c: Coincident(g338,g2)
    c: Coincident(g338,g336)
    c: Block(g3)
    c: Block(g339)
    c: Coincident(g340,g339)
    c: Coincident(g340,g3)
    c: Coincident(g341,g339)
    c: Coincident(g341,g3)
    c: Block(g341)
    c: Block(g340)
    c: Weight(g342) = 1
    c: Equal(g342,g343)
    c: Equal(g342,g344)
    c: InternalAlignment(g342,g345)
    c: InternalAlignment(g343,g345)
    c: InternalAlignment(g344,g345)
    c: InternalAlignment(g346,g345)
    c: InternalAlignment(g347,g345)
    c: Weight(g348) = 1
    c: Equal(g348,g349)
    c: Equal(g348,g350)
    c: InternalAlignment(g348,g351)
    c: InternalAlignment(g349,g351)
    c: InternalAlignment(g350,g351)
    c: InternalAlignment(g352,g351)
    c: InternalAlignment(g353,g351)
    c: Weight(g354) = 1
    c: Equal(g354,g355)
    c: Equal(g354,g356)
    c: InternalAlignment(g354,g357)
    c: InternalAlignment(g355,g357)
    c: InternalAlignment(g356,g357)
    c: InternalAlignment(g358,g357)
    c: InternalAlignment(g359,g357)
    c: Weight(g360) = 1
    c: Equal(g360,g361)
    c: Equal(g360,g362)
    c: InternalAlignment(g360,g363)
    c: InternalAlignment(g361,g363)
    c: InternalAlignment(g362,g363)
    c: InternalAlignment(g364,g363)
    c: InternalAlignment(g365,g363)
    c: Block(g363)
    c: Block(g357)
    c: Block(g351)
    c: Block(g345)
    c: Coincident(g366,g363)
    c: Coincident(g366,g345)
    c: Vertical(g366)
    c: Coincident(g367,g345)
    c: Coincident(g367,g351)
    c: Coincident(g368,g351)
    c: Coincident(g368,g357)
    c: Vertical(g368)
    c: Coincident(g369,g357)
    c: Coincident(g369,g363)
    c: Horizontal(g369)
    c: Vertical(g370)
    c: Coincident(g371,g0)
    c: Coincident(g371,g1)
    c: Horizontal(g371)
    c: Block(g371)
    c: Distance(g371) = 450
    c: Block(g370)
    c: Distance(g0) = 240
    c: Horizontal(g372)
    c: Distance(g372) = 12
    c: Vertical(g373)
    c: Distance(g373) = 12
    c: Coincident(g374,g372)
    c: Vertical(g374)
    c: Horizontal(g375)
    c: Vertical(g376)
    c: Distance(g376) = 6
    c: Coincident(g376,g372)
    c: Coincident(g375,g372)
    c: Block(g374)
    c: Coincident(g377,g374)
    c: Horizontal(g377)
    c: Distance(g377) = 6
    c: Vertical(g378)
    c: Distance(g378) = 3
    c: Vertical(g379)
    c: Distance(g379) = 3
    c: Coincident(g373,g378)
    c: Coincident(g385,g379)
    c: Weight(g380) = 1
    c: Equal(g380,g381)
    c: Coincident(g381,g375)
    c: Equal(g380,g382)
    c: Coincident(g382,g376)
    c: Equal(g380,g383)
    c: Coincident(g383,g377)
    c: Equal(g380,g384)
    c: Coincident(g385,g378)
    c: InternalAlignment(g380-g384 -> g385) x5
    c: InternalAlignment(g386,g385)
    c: InternalAlignment(g387,g385)
    c: InternalAlignment(g388,g385)
    c: Coincident(g389,g164)
    c: Coincident(g389,g158)
    c: Horizontal(g389)
    c: Block(g385)
    c: Vertical(g390)
    c: Distance(g390) = 12
    c: Horizontal(g391)
    c: Distance(g391) = 12
    c: Coincident(g392,g391)
    c: Vertical(g392)
    c: Distance(g392) = 12
    c: Horizontal(g393)
    c: Distance(g393) = 6
    c: Coincident(g393,g391)
    c: Vertical(g394)
    c: Distance(g394) = 6
    c: Coincident(g394,g391)
    c: Vertical(g395)
    c: Distance(g395) = 3
    c: Vertical(g396)
    c: Distance(g396) = 6
    c: Coincident(g396,g395)
    c: Coincident(g402,g395)
    c: Weight(g397) = 1
    c: Equal(g397,g398)
    c: Coincident(g398,g393)
    c: Equal(g397,g399)
    c: Coincident(g399,g394)
    c: Equal(g397,g400)
    c: Equal(g397,g401)
    c: Coincident(g402,g396)
    c: InternalAlignment(g397-g401 -> g402) x5
    c: InternalAlignment(g403,g402)
    c: InternalAlignment(g404,g402)
    c: InternalAlignment(g405,g402)
    c: Coincident(g406,g390)
    c: Coincident(g406,g170)
    c: Horizontal(g406)
    c: Block(g402)
    c: Coincident(g407,g176)
    c: Coincident(g407,g390)
    c: Horizontal(g407)
    c: Block(g406)
    c: Coincident(g409,g390)
    c: PointOnObject(g409,g153)
    c: Vertical(g409)
    c: Block(g410)
    c: Coincident(g411,g410)
    c: Vertical(g411)
    c: PointOnObject(g411,g40)
    c: Block(g411)
    c: Coincident(g412,g410)
    c: Vertical(g412)
    c: Block(g412)
    c: Vertical(g413)
    c: Distance(g413) = 3
    c: Equal(g380,g416) = 1
    c: Equal(g416,g417)
    c: InternalAlignment(g416,g418)
    c: InternalAlignment(g417,g418)
    c: InternalAlignment(g414,g418)
    c: InternalAlignment(g415,g418)
    c: InternalAlignment(g419,g418)
    c: Block(g418)
    c: Coincident(g419,g413)
    c: Coincident(g420,g418)
    c: PointOnObject(g420,g150)
    c: Vertical(g420)
    c: PointOnObject(g421,g211)
    c: Block(g421)
    c: Distance(g422) = 3
    c: Block(g422)
    c: Distance(g423) = 3
    c: Parallel(g423,g422)
    c: Coincident(g423,g422)
    c: Coincident(g424,g422)
FEATURE [Part::Extrusion] Extrude005
  Base = -> Sketch003
  Dir = (0,0,1)
  DirMode = 2
  FaceMakerClass = Part::FaceMakerBullseye
  LengthFwd = 24
  LengthRev = 0
  Solid = true
  Symmetric = false
